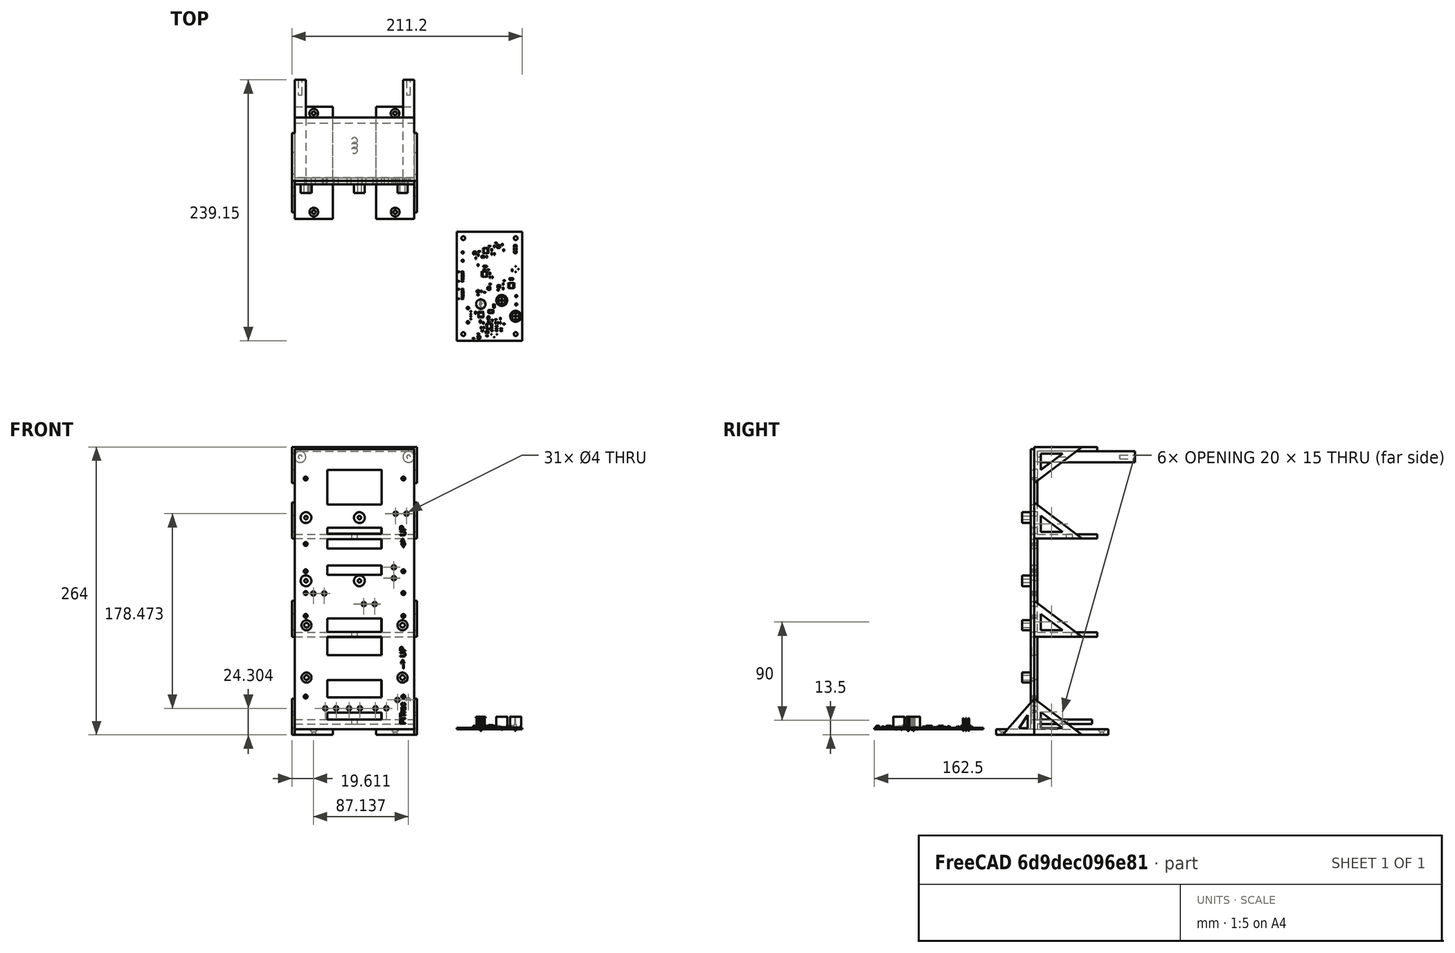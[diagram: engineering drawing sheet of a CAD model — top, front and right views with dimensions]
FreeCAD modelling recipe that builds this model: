
FCSTD DOCUMENT  (FreeCAD 1.0R39109 (Git))
Label: Tower
License: All rights reserved
LicenseURL: http://en.wikipedia.org/wiki/All_rights_reserved
objects: Part::Feature×73, Sketcher::SketchObject×17, PartDesign::Pad×9, PartDesign::Plane×9, PartDesign::Pocket×5, PartDesign::Hole×3, PartDesign::Mirrored×2, PartDesign::Body×2, App::Part×2, App::Link×1, Part::Part2DObjectPython×1
note: 174 computed .brp shape members not serialized (recipe doc carries the construction recipe); baked Part::Feature solids carry a one-line shape summary decoded from their .brp
EXTERNAL_REF file=../Master Document.FCStd obj=Spreadsheet

FEATURE [App::Link] Link  label="Monitor Chassis Parameters"
  LinkedObject = -> <external ../Master Document.FCStd>#Spreadsheet
FEATURE [Sketcher::SketchObject] Sketch  label="Backplate Sketch"
  ArcFitTolerance = 1e-06
  AttachmentSupport = -> [XZ_Plane001]
  FullyConstrained = false
  MakeInternals = false
  MapMode = 5
  Placement = pos=(0,0,0) rot=(1,0,0;1.5708rad)
  expr: Constraints[10] = <<Monitor Chassis Parameters>>.GSBackPlateBoltDiameter
  expr: Constraints[11] = <<Monitor Chassis Parameters>>.GSComputeBoardWidth / 2 - <<Monitor Chassis Parameters>>.GSBackPlateOuterHolesInsetFromSide
  expr: Constraints[129] = <<Monitor Chassis Parameters>>.GSTowerTieDownHoleSeparation
  expr: Constraints[15] = <<Monitor Chassis Parameters>>.GSBackPlateWidthIncrement
  expr: Constraints[55] = <<Monitor Chassis Parameters>>.GSBackPlateLengthIncrement
  expr: Constraints[59] = <<Monitor Chassis Parameters>>.GSBackPlateWidth
  expr: Constraints[71] = 1.5 * <<Monitor Chassis Parameters>>.GSBackPlateMinimumSpanWidth
  expr: Constraints[72] = 1.5 * <<Monitor Chassis Parameters>>.GSBackPlateMinimumSpanWidth
  expr: Constraints[7] = <<Monitor Chassis Parameters>>.GSComputeBoardHeight
  expr: Constraints[80] = <<Monitor Chassis Parameters>>.GSBackPlateLengthIncrement
  expr: Constraints[8] = <<Monitor Chassis Parameters>>.GSComputeBoardWidth
  expr: Constraints[97] = <<Monitor Chassis Parameters>>.GSTowerTieDownHoleDiameter
  expr: Constraints[98] = <<Monitor Chassis Parameters>>.GSTowerTieDownHoleDiameter
  expr: Constraints[99] = <<Monitor Chassis Parameters>>.GSTowerTieDownHoleSeparation
  expr: Constraints[9] = <<Monitor Chassis Parameters>>.GSComputeBoardWidth / 2
  sketch-geometry (63):
    g0: LineSegment [constr] StartX=-50.8 StartY=24.4067 StartZ=0 EndX=50.8 EndY=24.4067 EndZ=0
    g1: LineSegment [constr] StartX=50.8 StartY=24.4067 StartZ=0 EndX=50.8 EndY=253.007 EndZ=0
    g2: LineSegment [constr] StartX=50.8 StartY=253.007 StartZ=0 EndX=-50.8 EndY=253.007 EndZ=0
    g3: LineSegment [constr] StartX=-50.8 StartY=253.007 StartZ=0 EndX=-50.8 EndY=24.4067 EndZ=0
    g4: Circle CenterX=46.99 CenterY=45.5 CenterZ=0 NormalX=0 NormalY=0 NormalZ=1 AngleXU=0 Radius=1.4
    g5: LineSegment StartX=-54.8 StartY=257.007 StartZ=0 EndX=-54.8 EndY=20.4067 EndZ=0
    g6: LineSegment [constr] StartX=-54.8 StartY=20.4067 StartZ=0 EndX=54.8 EndY=20.4067 EndZ=0
    g7: LineSegment StartX=24.8 StartY=141.727 StartZ=0 EndX=-24.8 EndY=141.727 EndZ=0
    g8: LineSegment StartX=-24.8 StartY=141.727 StartZ=0 EndX=-24.8 EndY=150.228 EndZ=0
    g9: LineSegment StartX=-24.8 StartY=150.228 StartZ=0 EndX=24.8 EndY=150.228 EndZ=0
    g10: LineSegment StartX=24.8 StartY=150.228 StartZ=0 EndX=24.8 EndY=141.727 EndZ=0
    g11: LineSegment StartX=24.8 StartY=238.088 StartZ=0 EndX=-24.8 EndY=238.088 EndZ=0
    g12: LineSegment StartX=-24.8 StartY=238.088 StartZ=0 EndX=-24.8 EndY=206.336 EndZ=0
    g13: LineSegment StartX=-24.8 StartY=206.336 StartZ=0 EndX=24.8 EndY=206.336 EndZ=0
    g14: LineSegment StartX=24.8 StartY=206.336 StartZ=0 EndX=24.8 EndY=238.088 EndZ=0
    g15: LineSegment StartX=-24.8 StartY=184.895 StartZ=0 EndX=-24.8 EndY=179.263 EndZ=0
    g16: LineSegment StartX=-24.8 StartY=179.263 StartZ=0 EndX=24.8 EndY=179.263 EndZ=0
    g17: LineSegment StartX=24.8 StartY=179.263 StartZ=0 EndX=24.8 EndY=184.895 EndZ=0
    g18: LineSegment StartX=24.8 StartY=184.895 StartZ=0 EndX=-24.8 EndY=184.895 EndZ=0
    g19: LineSegment StartX=-24.8 StartY=84.8648 StartZ=0 EndX=-24.8 EndY=68.0887 EndZ=0
    g20: LineSegment StartX=-24.8 StartY=68.0887 StartZ=0 EndX=24.8 EndY=68.0887 EndZ=0
    g21: LineSegment StartX=24.8 StartY=68.0887 StartZ=0 EndX=24.8 EndY=84.8648 EndZ=0
    g22: LineSegment StartX=24.8 StartY=84.8648 StartZ=0 EndX=-24.8 EndY=84.8648 EndZ=0
    g23: LineSegment StartX=-24.8 StartY=45.1663 StartZ=0 EndX=-24.8 EndY=29.2968 EndZ=0
    g24: LineSegment StartX=24.8 StartY=29.2968 StartZ=0 EndX=24.8 EndY=45.1663 EndZ=0
    g25: LineSegment StartX=54.8 StartY=20.4067 StartZ=0 EndX=54.8 EndY=257.007 EndZ=0
    g26: LineSegment StartX=-54.8 StartY=257.007 StartZ=0 EndX=54.8 EndY=257.007 EndZ=0
    g27: LineSegment StartX=-54.8 StartY=20.4067 StartZ=0 EndX=-54.8 EndY=0 EndZ=0
    g28: LineSegment StartX=-54.8 StartY=0 StartZ=0 EndX=54.8 EndY=0 EndZ=0
    g29: LineSegment StartX=54.8 StartY=0 StartZ=0 EndX=54.8 EndY=20.4067 EndZ=0
    g30: LineSegment [constr] StartX=54.8 StartY=20.4067 StartZ=0 EndX=-54.8 EndY=20.4067 EndZ=0
    g31: LineSegment StartX=-24.8 StartY=45.1663 StartZ=0 EndX=24.8 EndY=45.1663 EndZ=0
    g32: LineSegment StartX=-24.8 StartY=29.2968 StartZ=0 EndX=24.8 EndY=29.2968 EndZ=0
    g33: LineSegment StartX=-24.8 StartY=15.5143 StartZ=0 EndX=-24.8 EndY=9.05652 EndZ=0
    g34: LineSegment StartX=-24.8 StartY=9.05652 StartZ=0 EndX=24.8 EndY=9.05652 EndZ=0
    g35: LineSegment StartX=24.8 StartY=9.05652 StartZ=0 EndX=24.8 EndY=15.5143 EndZ=0
    g36: LineSegment StartX=24.8 StartY=15.5143 StartZ=0 EndX=-24.8 EndY=15.5143 EndZ=0
    g37: Circle CenterX=37.7226 CenterY=197.777 CenterZ=0 NormalX=0 NormalY=0 NormalZ=1 AngleXU=0 Radius=2
    g38: Circle CenterX=47.7226 CenterY=197.777 CenterZ=0 NormalX=0 NormalY=0 NormalZ=1 AngleXU=0 Radius=2
    g39: Circle CenterX=-4.99066 CenterY=19.304 CenterZ=0 NormalX=0 NormalY=0 NormalZ=1 AngleXU=0 Radius=2
    g40: Circle CenterX=5.00934 CenterY=19.304 CenterZ=0 NormalX=0 NormalY=0 NormalZ=1 AngleXU=0 Radius=2
    g41: Circle CenterX=19.2048 CenterY=19.304 CenterZ=0 NormalX=0 NormalY=0 NormalZ=1 AngleXU=0 Radius=2
    g42: Circle CenterX=29.2048 CenterY=19.304 CenterZ=0 NormalX=0 NormalY=0 NormalZ=1 AngleXU=0 Radius=2
    g43: Circle CenterX=39.3678 CenterY=26.9682 CenterZ=0 NormalX=0 NormalY=0 NormalZ=1 AngleXU=0 Radius=2
    g44: Circle CenterX=49.3678 CenterY=26.9682 CenterZ=0 NormalX=0 NormalY=0 NormalZ=1 AngleXU=0 Radius=2
    g45: Circle CenterX=-37.7708 CenterY=124.614 CenterZ=0 NormalX=0 NormalY=0 NormalZ=1 AngleXU=0 Radius=2
    g46: Circle CenterX=-27.7708 CenterY=124.614 CenterZ=0 NormalX=0 NormalY=0 NormalZ=1 AngleXU=0 Radius=2
    g47: Circle CenterX=-26.8243 CenterY=19.304 CenterZ=0 NormalX=0 NormalY=0 NormalZ=1 AngleXU=0 Radius=2
    g48: Circle CenterX=-16.8243 CenterY=19.304 CenterZ=0 NormalX=0 NormalY=0 NormalZ=1 AngleXU=0 Radius=2
    g49: Circle CenterX=36.1106 CenterY=138.665 CenterZ=0 NormalX=0 NormalY=0 NormalZ=1 AngleXU=0 Radius=2
    g50: Circle CenterX=36.1106 CenterY=148.665 CenterZ=0 NormalX=0 NormalY=0 NormalZ=1 AngleXU=0 Radius=2
    g51: Circle CenterX=49.3678 CenterY=26.9682 CenterZ=0 NormalX=0 NormalY=0 NormalZ=1 AngleXU=0 Radius=2
    g52: Circle CenterX=8.52821 CenterY=114.871 CenterZ=0 NormalX=0 NormalY=0 NormalZ=1 AngleXU=0 Radius=2
    g53: Circle CenterX=18.5282 CenterY=114.871 CenterZ=0 NormalX=0 NormalY=0 NormalZ=1 AngleXU=0 Radius=2
    g54: Circle CenterX=49.3678 CenterY=26.9682 CenterZ=0 NormalX=0 NormalY=0 NormalZ=1 AngleXU=0 Radius=2
    g55: LineSegment StartX=-24.8 StartY=174.457 StartZ=0 EndX=-24.8 EndY=165.919 EndZ=0
    g56: LineSegment StartX=-24.8 StartY=165.919 StartZ=0 EndX=24.8 EndY=165.919 EndZ=0
    g57: LineSegment StartX=24.8 StartY=165.919 StartZ=0 EndX=24.8 EndY=174.457 EndZ=0
    g58: LineSegment StartX=24.8 StartY=174.457 StartZ=0 EndX=-24.8 EndY=174.457 EndZ=0
    g59: LineSegment StartX=-24.8 StartY=101.627 StartZ=0 EndX=-24.8 EndY=89.2697 EndZ=0
    g60: LineSegment StartX=-24.8 StartY=89.2697 StartZ=0 EndX=24.8 EndY=89.2697 EndZ=0
    g61: LineSegment StartX=24.8 StartY=89.2697 StartZ=0 EndX=24.8 EndY=101.627 EndZ=0
    g62: LineSegment StartX=24.8 StartY=101.627 StartZ=0 EndX=-24.8 EndY=101.627 EndZ=0
  constraints (152):
    c: Coincident(g0,g1)
    c: Coincident(g1,g2)
    c: Coincident(g2,g3)
    c: Coincident(g3,g0)
    c: Horizontal(g2)
    c: Vertical(g1)
    c: Vertical(g3)
    c: DistanceY(g0,g2) = 228.6
    c: DistanceX(g0,g0) = 101.6
    c: DistanceX(g0,g-1) = 50.8
    c: Diameter(g4) = 2.8
    c: DistanceX(g-1,g4) = 46.99
    c: Coincident(g5,g6)
    c: Vertical(g5)
    c: Horizontal(g6)
    c: DistanceX(g5,g0) = 4
    c: Horizontal(g0)
    c: Coincident(g7,g8)
    c: Coincident(g8,g9)
    c: Coincident(g9,g10)
    c: Coincident(g10,g7)
    c: Horizontal(g7)
    c: Vertical(g8)
    c: Vertical(g10)
    c: Coincident(g11,g12)
    c: Coincident(g12,g13)
    c: Coincident(g13,g14)
    c: Coincident(g14,g11)
    c: Horizontal(g11)
    c: Horizontal(g13)
    c: Vertical(g12)
    c: Vertical(g14)
    c: Coincident(g15,g16)
    c: Coincident(g16,g17)
    c: Coincident(g17,g18)
    c: Coincident(g18,g15)
    c: Vertical(g15)
    c: Vertical(g17)
    c: Horizontal(g16)
    c: Coincident(g19,g20)
    c: Coincident(g20,g21)
    c: Coincident(g21,g22)
    c: Coincident(g22,g19)
    c: Vertical(g19)
    c: Vertical(g21)
    c: Horizontal(g20)
    c: Horizontal(g22)
    c: Vertical(g23)
    c: Vertical(g24)
    c: Vertical(g15,g19)
    c: Vertical(g19,g23)
    c: Vertical(g7,g21)
    c: Vertical(g21,g24)
    c: Coincident(g25,g6)
    c: Vertical(g25)
    c: DistanceY(g1,g25) = 4
    c: Horizontal(g5,g25)
    c: Coincident(g26,g5)
    c: Coincident(g26,g25)
    c: DistanceX(g5,g6) = 109.6
    c: Coincident(g27,g28)
    c: Coincident(g28,g29)
    c: Coincident(g29,g30)
    c: Coincident(g30,g27)
    c: Vertical(g27)
    c: Vertical(g29)
    c: Horizontal(g28)
    c: Horizontal(g30)
    c: Coincident(g27,g5)
    c: Horizontal(g28,g-1)
    c: Vertical(g29,g6)
    c: DistanceX(g5,g11) = 30
    c: DistanceX(g11,g25) = 30
    c: Horizontal(g9)
    c: Coincident(g31,g23)
    c: Coincident(g31,g24)
    c: Horizontal(g31)
    c: Vertical(g11,g15)
    c: Vertical(g11,g9)
    c: Vertical(g16,g9)
    c: DistanceY(g5,g0) = 4
    c: Coincident(g32,g23)
    c: Coincident(g32,g24)
    c: Horizontal(g32)
    c: Horizontal(g18)
    c: Vertical(g15,g8)
    c: Coincident(g33,g34)
    c: Coincident(g34,g35)
    c: Coincident(g35,g36)
    c: Coincident(g36,g33)
    c: Vertical(g33)
    c: Vertical(g35)
    c: Horizontal(g34)
    c: Horizontal(g36)
    c: Vertical(g23,g33)
    c: Vertical(g24,g35)
    c: Horizontal(g37,g38)
    c: Diameter(g37) = 4
    c: Diameter(g38) = 4
    c: DistanceX(g37,g38) = 10
    c: Horizontal(g39,g40)
    c: Diameter(g39) = 4
    c: Diameter(g40) = 4
    c: DistanceX(g39,g40) = 10
    c: Horizontal(g41,g42)
    c: Diameter(g41) = 4
    c: Diameter(g42) = 4
    c: DistanceX(g41,g42) = 10
    c: Horizontal(g43,g44)
    c: Diameter(g43) = 4
    c: Diameter(g44) = 4
    c: DistanceX(g43,g44) = 10
    c: Horizontal(g45,g46)
    c: Diameter(g45) = 4
    c: Diameter(g46) = 4
    c: DistanceX(g45,g46) = 10
    c: Horizontal(g47,g48)
    c: Diameter(g47) = 4
    c: Diameter(g48) = 4
    c: DistanceX(g47,g48) = 10
    c: Diameter(g49) = 4
    c: Diameter(g50) = 4
    c: Diameter(g51) = 4
    c: Horizontal(g52,g53)
    c: Diameter(g52) = 4
    c: Diameter(g53) = 4
    c: DistanceX(g52,g53) = 10
    c: Diameter(g54) = 4
    c: Vertical(g50,g49)
    c: DistanceY(g49,g50) = 10
    c: Horizontal(g48,g39)
    c: Horizontal(g40,g41)
    c: Coincident(g55,g56)
    c: Coincident(g56,g57)
    c: Coincident(g57,g58)
    c: Coincident(g58,g55)
    c: Vertical(g55)
    c: Vertical(g57)
    c: Horizontal(g56)
    c: Horizontal(g58)
    c: Vertical(g8,g55)
    c: Vertical(g9,g56)
    c: Coincident(g59,g60)
    c: Coincident(g60,g61)
    c: Coincident(g61,g62)
    c: Coincident(g62,g59)
    c: Vertical(g59)
    c: Vertical(g61)
    c: Horizontal(g60)
    c: Horizontal(g62)
    c: Vertical(g20,g60)
    c: Vertical(g19,g59)
FEATURE [PartDesign::Pad] Pad  label="Backplate Pad"
  Direction = (0,-1,2e-16)
  Length = 3
  Length2 = 10
  Placement = pos=(0,0,0) rot=(1,0,0;1.5708rad)
  Profile = -> Sketch
  ReferenceAxis = -> Sketch [N_Axis]
  Reversed = true
  Suppressed = false
  Type = 0
  expr: Length = <<Monitor Chassis Parameters>>.GSBackPlateThickness
FEATURE [Sketcher::SketchObject] Sketch001  label="Backplate Risers Sketch"
  ArcFitTolerance = 1e-06
  AttachmentSupport = -> [XZ_Plane001]
  FullyConstrained = false
  MakeInternals = false
  MapMode = 5
  Placement = pos=(0,0,0) rot=(1,0,0;1.5708rad)
  expr: Constraints[12] = <<Monitor Chassis Parameters>>.GSPi5MountingRiserOutsideDiameter
  expr: Constraints[13] = <<Monitor Chassis Parameters>>.GSPi5MountingRiserOutsideDiameter
  expr: Constraints[14] = <<Monitor Chassis Parameters>>.GSPi5MountingRiserOutsideDiameter
  expr: Constraints[18] = <<Monitor Chassis Parameters>>.GSPi5MountingHoleCenterLength
  expr: Constraints[19] = <<Monitor Chassis Parameters>>.GSPi5MountingRiserOutsideDiameter
  expr: Constraints[21] = <<Monitor Chassis Parameters>>.GsPi5MountingHoleDiameter
  expr: Constraints[25] = <<Monitor Chassis Parameters>>.GSConnectorBoardMountingRiserOutsideDiameter
  expr: Constraints[26] = <<Monitor Chassis Parameters>>.GSConnectorBoardMountingHoleDiameter
  expr: Constraints[28] = <<Monitor Chassis Parameters>>.GSConnectorBoardMountingRiserOutsideDiameter
  expr: Constraints[29] = <<Monitor Chassis Parameters>>.GSConnectorBoardMountingHoleDiameter
  expr: Constraints[31] = <<Monitor Chassis Parameters>>.GSConnectorBoardMountingRiserOutsideDiameter
  expr: Constraints[32] = <<Monitor Chassis Parameters>>.GSConnectorBoardMountingHoleDiameter
  expr: Constraints[34] = <<Monitor Chassis Parameters>>.GSConnectorBoardMountingRiserOutsideDiameter
  expr: Constraints[35] = <<Monitor Chassis Parameters>>.GSConnectorBoardMountingHoleDiameter
  expr: Constraints[38] = <<Monitor Chassis Parameters>>.GsV2ConnectorBoardMountingHoleSeparationX
  expr: Constraints[39] = <<Monitor Chassis Parameters>>.GsV2ConnectorBoardMountingHoleSeparationY
  expr: Constraints[40] = 0.5 * <<Monitor Chassis Parameters>>.GSComputeBoardWidth - 0.5 * (<<Monitor Chassis Parameters>>.GSComputeBoardWidth - <<Monitor Chassis Parameters>>.GsV2ConnectorBoardMountingHoleSeparationX)
  expr: Constraints[41] = <<Monitor Chassis Parameters>>.GSPi5MountingHoleCenterWidth
  expr: Constraints[44] = 20 + 0.5 * <<Monitor Chassis Parameters>>.GSComputeBoardWidth - 0.5 * (<<Monitor Chassis Parameters>>.GSComputeBoardWidth - <<Monitor Chassis Parameters>>.GSPi5MountingHoleCenterWidth)
  expr: Constraints[5] = <<Monitor Chassis Parameters>>.GsPi5MountingHoleDiameter
  expr: Constraints[6] = <<Monitor Chassis Parameters>>.GsPi5MountingHoleDiameter
  expr: Constraints[7] = <<Monitor Chassis Parameters>>.GsPi5MountingHoleDiameter
  sketch-geometry (20):
    g0: LineSegment [constr] StartX=-50.8 StartY=20 StartZ=0 EndX=50.8 EndY=20 EndZ=0
    g1: LineSegment [constr] StartX=50.8 StartY=20 StartZ=0 EndX=50.8 EndY=248.6 EndZ=0
    g2: LineSegment [constr] StartX=50.8 StartY=248.6 StartZ=0 EndX=-50.8 EndY=248.6 EndZ=0
    g3: LineSegment [constr] StartX=-50.8 StartY=248.6 StartZ=0 EndX=-50.8 EndY=20 EndZ=0
    g4: Circle CenterX=-44.5 CenterY=136.223 CenterZ=0 NormalX=0 NormalY=0 NormalZ=1 AngleXU=0 Radius=1.575
    g5: Circle CenterX=4.5 CenterY=136.223 CenterZ=0 NormalX=0 NormalY=0 NormalZ=1 AngleXU=0 Radius=1.575
    g6: Circle CenterX=-44.5 CenterY=194.223 CenterZ=0 NormalX=0 NormalY=0 NormalZ=1 AngleXU=0 Radius=1.575
    g7: Circle CenterX=-44.5 CenterY=194.223 CenterZ=0 NormalX=0 NormalY=0 NormalZ=1 AngleXU=0 Radius=4.95
    g8: Circle CenterX=-44.5 CenterY=136.223 CenterZ=0 NormalX=0 NormalY=0 NormalZ=1 AngleXU=0 Radius=4.95
    g9: Circle CenterX=4.5 CenterY=136.223 CenterZ=0 NormalX=0 NormalY=0 NormalZ=1 AngleXU=0 Radius=4.95
    g10: Circle CenterX=4.5 CenterY=194.223 CenterZ=0 NormalX=0 NormalY=0 NormalZ=1 AngleXU=0 Radius=4.95
    g11: Circle CenterX=4.5 CenterY=194.223 CenterZ=0 NormalX=0 NormalY=0 NormalZ=1 AngleXU=0 Radius=1.575
    g12: Circle CenterX=-44 CenterY=47.4737 CenterZ=0 NormalX=0 NormalY=0 NormalZ=1 AngleXU=0 Radius=2.125
    g13: Circle CenterX=-44 CenterY=47.4737 CenterZ=0 NormalX=0 NormalY=0 NormalZ=1 AngleXU=0 Radius=4.625
    g14: Circle CenterX=44 CenterY=47.4737 CenterZ=0 NormalX=0 NormalY=0 NormalZ=1 AngleXU=0 Radius=2.125
    g15: Circle CenterX=44 CenterY=47.4737 CenterZ=0 NormalX=0 NormalY=0 NormalZ=1 AngleXU=0 Radius=4.625
    g16: Circle CenterX=44 CenterY=95.4737 CenterZ=0 NormalX=0 NormalY=0 NormalZ=1 AngleXU=0 Radius=2.125
    g17: Circle CenterX=44 CenterY=95.4737 CenterZ=0 NormalX=0 NormalY=0 NormalZ=1 AngleXU=0 Radius=4.625
    g18: Circle CenterX=-44 CenterY=95.4737 CenterZ=0 NormalX=0 NormalY=0 NormalZ=1 AngleXU=0 Radius=2.125
    g19: Circle CenterX=-44 CenterY=95.4737 CenterZ=0 NormalX=0 NormalY=0 NormalZ=1 AngleXU=0 Radius=4.625
  constraints (45):
    c: Coincident(g0,g1)
    c: Coincident(g1,g2)
    c: Coincident(g3,g0)
    c: Vertical(g1)
    c: Vertical(g3)
    c: Diameter(g4) = 3.15
    c: Diameter(g5) = 3.15
    c: Diameter(g6) = 3.15
    c: Horizontal(g0)
    c: Coincident(g7,g6)
    c: Coincident(g8,g4)
    c: Coincident(g9,g5)
    c: Diameter(g9) = 9.9
    c: Diameter(g8) = 9.9
    c: Diameter(g7) = 9.9
    c: Horizontal(g5,g4)
    c: Horizontal(g2,g1)
    c: Vertical(g6,g4)
    c: DistanceY(g4,g6) = 58
    c: Diameter(g10) = 9.9
    c: Coincident(g11,g10)
    c: Diameter(g11) = 3.15
    c: Horizontal(g10,g6)
    c: Vertical(g10,g5)
    c: Coincident(g13,g12)
    c: Diameter(g13) = 9.25
    c: Diameter(g12) = 4.25
    c: Coincident(g15,g14)
    c: Diameter(g15) = 9.25
    c: Diameter(g14) = 4.25
    c: Coincident(g17,g16)
    c: Diameter(g17) = 9.25
    c: Diameter(g16) = 4.25
    c: Coincident(g19,g18)
    c: Diameter(g19) = 9.25
    c: Diameter(g18) = 4.25
    c: Horizontal(g16,g18)
    c: Horizontal(g14,g12)
    c: DistanceX(g18,g16) = 88
    c: DistanceY(g12,g18) = 48
    c: DistanceX(g18,g-1) = 44
    c: DistanceX(g6,g10) = 49
    c: Vertical(g12,g18)
    c: Vertical(g16,g14)
    c: DistanceX(g4,g-1) = 44.5
FEATURE [PartDesign::Pad] Pad001  label="Backplate Risers Pad"
  BaseFeature = -> Pad
  Direction = (0,-1,2e-16)
  Length = 8
  Length2 = 10
  Placement = pos=(0,0,0) rot=(1,0,0;1.5708rad)
  Profile = -> Sketch001
  ReferenceAxis = -> Sketch001 [N_Axis]
  Suppressed = false
  Type = 0
  expr: Length = <<Monitor Chassis Parameters>>.GSBackPlateConnectorBoardVariantStandoffHeight
FEATURE [Sketcher::SketchObject] Sketch002  label="Backplate Foot Sketch"
  ArcFitTolerance = 1e-06
  AttachmentSupport = -> [XZ_Plane001]
  FullyConstrained = true
  MakeInternals = false
  MapMode = 5
  Placement = pos=(0,0,0) rot=(1,0,0;1.5708rad)
  expr: Constraints[11] = <<Monitor Chassis Parameters>>.GSTowerFeetThickness
  expr: Constraints[21] = <<Monitor Chassis Parameters>>.GSTowerFeetThickness
  expr: Constraints[22] = <<Monitor Chassis Parameters>>.GSBackPlateFootWidth
  expr: Constraints[23] = 0.5 * <<Monitor Chassis Parameters>>.GSBackPlateWidth
  expr: Constraints[8] = <<Monitor Chassis Parameters>>.GSBackPlateFootWidth
  expr: Constraints[9] = 0.5 * <<Monitor Chassis Parameters>>.GSBackPlateWidth
  sketch-geometry (8):
    g0: LineSegment StartX=-54.8 StartY=-5 StartZ=0 EndX=-19.8 EndY=-5 EndZ=0
    g1: LineSegment StartX=-19.8 StartY=-5 StartZ=0 EndX=-19.8 EndY=0 EndZ=0
    g2: LineSegment StartX=-19.8 StartY=0 StartZ=0 EndX=-54.8 EndY=0 EndZ=0
    g3: LineSegment StartX=-54.8 StartY=0 StartZ=0 EndX=-54.8 EndY=-5 EndZ=0
    g4: LineSegment StartX=54.8 StartY=-5 StartZ=0 EndX=54.8 EndY=0 EndZ=0
    g5: LineSegment StartX=54.8 StartY=0 StartZ=0 EndX=19.8 EndY=0 EndZ=0
    g6: LineSegment StartX=19.8 StartY=0 StartZ=0 EndX=19.8 EndY=-5 EndZ=0
    g7: LineSegment StartX=19.8 StartY=-5 StartZ=0 EndX=54.8 EndY=-5 EndZ=0
  constraints (24):
    c: Coincident(g0,g1)
    c: Coincident(g1,g2)
    c: Coincident(g2,g3)
    c: Coincident(g3,g0)
    c: Horizontal(g0)
    c: Horizontal(g2)
    c: Vertical(g1)
    c: Vertical(g3)
    c: DistanceX(g2,g1) = 35
    c: DistanceX(g2,g-1) = 54.8
    c: Horizontal(g2,g-1)
    c: DistanceY(g0,g2) = 5
    c: Coincident(g4,g5)
    c: Coincident(g5,g6)
    c: Coincident(g6,g7)
    c: Coincident(g7,g4)
    c: Vertical(g4)
    c: Vertical(g6)
    c: Horizontal(g5)
    c: Horizontal(g7)
    c: Horizontal(g5,g-1)
    c: DistanceY(g4,g4) = 5
    c: DistanceX(g6,g4) = 35
    c: DistanceX(g-1,g4) = 54.8
FEATURE [PartDesign::Pad] Pad002  label="Backplate Foot Pad"
  BaseFeature = -> Pad001
  Direction = (0,-1,2e-16)
  Length = 32
  Length2 = 3
  Placement = pos=(0,0,0) rot=(1,0,0;1.5708rad)
  Profile = -> Sketch002
  ReferenceAxis = -> Sketch002 [N_Axis]
  Suppressed = false
  Type = 4
  expr: Length = <<Monitor Chassis Parameters>>.GSBackPlateFootLengthBackward
  expr: Length2 = <<Monitor Chassis Parameters>>.GSBackPlateThickness
FEATURE [Sketcher::SketchObject] Sketch003  label="Backplate Foot Screw Holes Sketch"
  ArcFitTolerance = 1e-06
  AttachmentSupport = -> [XY_Plane001]
  FullyConstrained = true
  MakeInternals = false
  MapMode = 5
  expr: Constraints[0] = 0.8 * <<Monitor Chassis Parameters>>.GSBackPlateFootLengthBackward
  expr: Constraints[1] = 0.5 * <<Monitor Chassis Parameters>>.GSBackPlateWidth - 0.5 * <<Monitor Chassis Parameters>>.GSBackPlateFootWidth
  expr: Constraints[2] = 0.5 * <<Monitor Chassis Parameters>>.GSBackPlateWidth - 0.5 * <<Monitor Chassis Parameters>>.GSBackPlateFootWidth
  expr: Constraints[3] = <<Monitor Chassis Parameters>>.GSTowerFeetScrewDiameter
  expr: Constraints[4] = <<Monitor Chassis Parameters>>.GSTowerFeetScrewDiameter
  sketch-geometry (2):
    g0: Circle CenterX=-37.3 CenterY=-25.6 CenterZ=0 NormalX=0 NormalY=0 NormalZ=1 AngleXU=0 Radius=1.7
    g1: Circle CenterX=37.3 CenterY=-25.6 CenterZ=0 NormalX=0 NormalY=0 NormalZ=1 AngleXU=0 Radius=1.7
  constraints (6):
    c: DistanceY(g0,g-1) = 25.6
    c: DistanceX(g0,g-1) = 37.3
    c: DistanceX(g-1,g1) = 37.3
    c: Diameter(g0) = 3.4
    c: Diameter(g1) = 3.4
    c: Horizontal(g1,g0)
FEATURE [PartDesign::Hole] Hole  label="Backplate Foot Screw Holes"
  BaseFeature = -> Pad002
  CustomThreadClearance = 0
  Depth = 25
  DepthType = 0
  Diameter = 3.4
  DrillForDepth = false
  DrillPoint = 1
  DrillPointAngle = 118
  HoleCutCountersinkAngle = 90
  HoleCutCustomValues = false
  HoleCutDepth = 0
  HoleCutDiameter = 8
  HoleCutType = 2
  ModelThread = false
  Placement = pos=(0,0,0) rot=(1,0,0;1.5708rad)
  Profile = -> Sketch003
  Suppressed = false
  Tapered = false
  TaperedAngle = 90
  ThreadClass = 0
  ThreadDepth = 25
  ThreadDepthType = 0
  ThreadDirection = 0
  ThreadFit = 0
  ThreadSize = 0
  ThreadType = 0
  Threaded = false
  UseCustomThreadClearance = false
  expr: Diameter = <<Monitor Chassis Parameters>>.GSTowerFeetScrewDiameter
  expr: HoleCutDiameter = <<Monitor Chassis Parameters>>.GSM4BoltCountersinkDiameter
FEATURE [PartDesign::Plane] DatumPlane
  AttachmentOffset = pos=(0,0,54.8) rot=(0,0,1;0rad)
  AttachmentSupport = -> [YZ_Plane001]
  Length = 73.939
  MapMode = 5
  Placement = pos=(54.8,0,0) rot=(0.57735,0.57735,0.57735;2.0944rad)
  ResizeMode = 0
  Width = 245.788
  expr: .AttachmentOffset.Base.z = 0.5 * <<Monitor Chassis Parameters>>.GSBackPlateWidth
FEATURE [Sketcher::SketchObject] Sketch004  label="Foot Support Corner Sketch"
  ArcFitTolerance = 1e-06
  AttachmentSupport = -> [DatumPlane]
  FullyConstrained = true
  MakeInternals = false
  MapMode = 5
  Placement = pos=(54.8,0,0) rot=(0.57735,0.57735,0.57735;2.0944rad)
  expr: Constraints[14] = <<Monitor Chassis Parameters>>.GSSideCornerCutoutInset
  expr: Constraints[15] = <<Monitor Chassis Parameters>>.GSSideCornerCutoutInset
  expr: Constraints[16] = 2.5 * <<Monitor Chassis Parameters>>.GSSideCornerCutoutInset
  expr: Constraints[17] = 2.5 * <<Monitor Chassis Parameters>>.GSSideCornerCutoutInset
  expr: Constraints[1] = <<Monitor Chassis Parameters>>.GSBackPlateThickness
  expr: Constraints[4] = <<Monitor Chassis Parameters>>.GSTowerFeetThickness
  expr: Constraints[7] = 0.9 * <<Monitor Chassis Parameters>>.GSBackPlateFootLengthBackward
  expr: Constraints[8] = 0.6 * <<Monitor Chassis Parameters>>.GSTowerFloorDepth
  sketch-geometry (6):
    g0: LineSegment StartX=-25.8 StartY=-5 StartZ=0 EndX=3 EndY=-5 EndZ=0
    g1: LineSegment StartX=3 StartY=28 StartZ=0 EndX=3 EndY=-5 EndZ=0
    g2: LineSegment StartX=-25.8 StartY=-5 StartZ=0 EndX=3 EndY=28 EndZ=0
    g3: LineSegment StartX=-10.8 StartY=1 StartZ=0 EndX=-3 EndY=13 EndZ=0
    g4: LineSegment StartX=-3 StartY=13 StartZ=0 EndX=-3 EndY=1 EndZ=0
    g5: LineSegment StartX=-10.8 StartY=1 StartZ=0 EndX=-3 EndY=1 EndZ=0
  constraints (18):
    c: Horizontal(g0)
    c: DistanceX(g-1,g0) = 3
    c: Coincident(g1,g0)
    c: Vertical(g1)
    c: DistanceY(g0,g-1) = 5
    c: Coincident(g2,g0)
    c: Coincident(g2,g1)
    c: DistanceX(g0,g0) = 28.8
    c: DistanceY(g0,g1) = 33
    c: Coincident(g4,g3)
    c: Vertical(g4)
    c: Coincident(g5,g3)
    c: Coincident(g5,g4)
    c: Horizontal(g5)
    c: DistanceY(g0,g4) = 6
    c: DistanceX(g4,g0) = 6
    c: DistanceX(g0,g3) = 15
    c: DistanceY(g3,g1) = 15
FEATURE [PartDesign::Pad] Pad003  label="Foot Support Corner Pad"
  BaseFeature = -> Hole
  Direction = (1,0,0)
  Length = 2.5
  Length2 = 10
  Placement = pos=(0,0,0) rot=(1,0,0;1.5708rad)
  Profile = -> Sketch004
  ReferenceAxis = -> Sketch004 [N_Axis]
  Suppressed = false
  Type = 0
  expr: Length = <<Monitor Chassis Parameters>>.GSSideCornerThickness
FEATURE [PartDesign::Mirrored] Mirrored  label="Foot Support Corner Mirrored"
  BaseFeature = -> Pad003
  MirrorPlane = -> YZ_Plane001
  Originals = -> [Pad003]
  Placement = pos=(0,0,0) rot=(1,0,0;1.5708rad)
  Suppressed = false
  TransformMode = 0
FEATURE [PartDesign::Plane] DatumPlane001
  AttachmentOffset = pos=(0,0,54.8) rot=(0,0,1;0rad)
  AttachmentSupport = -> [YZ_Plane002]
  Length = 82.8329
  MapMode = 5
  Placement = pos=(54.8,0,0) rot=(0.57735,0.57735,0.57735;2.0944rad)
  ResizeMode = 0
  Width = 201.085
  expr: .AttachmentOffset.Base.z = 0.5 * <<Monitor Chassis Parameters>>.GSBackPlateWidth
FEATURE [Sketcher::SketchObject] Sketch005  label="Frontplate Sketch"
  ArcFitTolerance = 1e-06
  AttachmentSupport = -> [XZ_Plane002]
  FullyConstrained = false
  MakeInternals = false
  MapMode = 5
  Placement = pos=(0,0,0) rot=(1,0,0;1.5708rad)
  expr: Constraints[103] = <<Monitor Chassis Parameters>>.GSTowerLayerJoinScrewDiameter
  expr: Constraints[104] = <<Monitor Chassis Parameters>>.GSTowerLayerJoinScrewDiameter
  expr: Constraints[106] = <<Monitor Chassis Parameters>>.GSTowerLayerJoinScrewHeightFromFoot_1
  expr: Constraints[107] = <<Monitor Chassis Parameters>>.GSTowerLayerJoinScrewHeightFromFoot_3
  expr: Constraints[109] = <<Monitor Chassis Parameters>>.GSTowerLayerJoinScrewHeightFromFoot_4
  expr: Constraints[110] = <<Monitor Chassis Parameters>>.GSTowerLayerJoinScrewHeightFromFoot_5
  expr: Constraints[112] = <<Monitor Chassis Parameters>>.GSTowerLayerJoinScrewDiameter
  expr: Constraints[113] = <<Monitor Chassis Parameters>>.GSTowerLayerJoinScrewDiameter
  expr: Constraints[116] = <<Monitor Chassis Parameters>>.GSTowerLayerJoinScrewHeightFromFoot_6
  expr: Constraints[128] = <<Monitor Chassis Parameters>>.GSTowerLayerJoinScrewDiameter
  expr: Constraints[133] = <<Monitor Chassis Parameters>>.GSTowerLayerJoinScrewHeightFromFoot_2
  expr: Constraints[134] = <<Monitor Chassis Parameters>>.GSTowerTieDownHoleDiameter
  expr: Constraints[135] = <<Monitor Chassis Parameters>>.GSTowerTieDownHoleDiameter
  expr: Constraints[13] = <<Monitor Chassis Parameters>>.GSBackPlateWidthIncrement
  expr: Constraints[141] = <<Monitor Chassis Parameters>>.GSTowerTieDownHoleSeparation
  expr: Constraints[60] = <<Monitor Chassis Parameters>>.GSBackPlateLengthIncrement
  expr: Constraints[64] = <<Monitor Chassis Parameters>>.GSBackPlateWidth
  expr: Constraints[65] = <<Monitor Chassis Parameters>>.GSBackPlateVerticalOffset
  expr: Constraints[7] = <<Monitor Chassis Parameters>>.GSComputeBoardHeight
  expr: Constraints[84] = 1.5 * <<Monitor Chassis Parameters>>.GSFrontPlateMinimumSpanWidth
  expr: Constraints[85] = 1.5 * <<Monitor Chassis Parameters>>.GSFrontPlateMinimumSpanWidth
  expr: Constraints[89] = <<Monitor Chassis Parameters>>.GSTowerFourthFloorHeight + <<Monitor Chassis Parameters>>.GSTowerFloorThickness
  expr: Constraints[8] = <<Monitor Chassis Parameters>>.GSComputeBoardWidth
  expr: Constraints[90] = <<Monitor Chassis Parameters>>.GSTowerLayerJoinScrewDiameter
  expr: Constraints[91] = <<Monitor Chassis Parameters>>.GSTowerLayerJoinScrewDiameter
  expr: Constraints[93] = <<Monitor Chassis Parameters>>.GSTowerLayerJoinScrewInset
  expr: Constraints[94] = <<Monitor Chassis Parameters>>.GSTowerLayerJoinScrewInset
  expr: Constraints[95] = <<Monitor Chassis Parameters>>.GSTowerLayerJoinScrewDiameter
  expr: Constraints[96] = <<Monitor Chassis Parameters>>.GSTowerLayerJoinScrewDiameter
  expr: Constraints[98] = <<Monitor Chassis Parameters>>.GSTowerLayerJoinScrewDiameter
  expr: Constraints[99] = <<Monitor Chassis Parameters>>.GSTowerLayerJoinScrewDiameter
  expr: Constraints[9] = <<Monitor Chassis Parameters>>.GSComputeBoardWidth / 2
  sketch-geometry (75):
    g0: LineSegment [constr] StartX=-50.8 StartY=24 StartZ=0 EndX=50.8 EndY=24 EndZ=0
    g1: LineSegment [constr] StartX=50.8 StartY=24 StartZ=0 EndX=50.8 EndY=252.6 EndZ=0
    g2: LineSegment [constr] StartX=50.8 StartY=252.6 StartZ=0 EndX=-50.8 EndY=252.6 EndZ=0
    g3: LineSegment [constr] StartX=-50.8 StartY=252.6 StartZ=0 EndX=-50.8 EndY=24 EndZ=0
    g4: LineSegment StartX=-54.8 StartY=256.6 StartZ=0 EndX=-54.8 EndY=20 EndZ=0
    g5: LineSegment [constr] StartX=-54.8 StartY=20 StartZ=0 EndX=54.8 EndY=20 EndZ=0
    g6: LineSegment StartX=24.8 StartY=185.058 StartZ=0 EndX=-24.8 EndY=185.058 EndZ=0
    g7: LineSegment StartX=-24.8 StartY=185.058 StartZ=0 EndX=-24.8 EndY=179.38 EndZ=0
    g8: LineSegment StartX=-24.8 StartY=179.38 StartZ=0 EndX=24.8 EndY=179.38 EndZ=0
    g9: LineSegment StartX=24.8 StartY=179.38 StartZ=0 EndX=24.8 EndY=185.058 EndZ=0
    g10: LineSegment StartX=24.8 StartY=141.478 StartZ=0 EndX=-24.8 EndY=141.478 EndZ=0
    g11: LineSegment StartX=-24.8 StartY=141.478 StartZ=0 EndX=-24.8 EndY=150.178 EndZ=0
    g12: LineSegment StartX=-24.8 StartY=150.178 StartZ=0 EndX=24.8 EndY=150.178 EndZ=0
    g13: LineSegment StartX=24.8 StartY=150.178 StartZ=0 EndX=24.8 EndY=141.478 EndZ=0
    g14: LineSegment StartX=24.8 StartY=238.453 StartZ=0 EndX=-24.9755 EndY=238.453 EndZ=0
    g15: LineSegment StartX=-24.9755 StartY=238.453 StartZ=0 EndX=-24.9755 EndY=206.288 EndZ=0
    g16: LineSegment StartX=-24.9755 StartY=206.288 StartZ=0 EndX=24.8 EndY=206.288 EndZ=0
    g17: LineSegment StartX=24.8 StartY=206.288 StartZ=0 EndX=24.8 EndY=238.453 EndZ=0
    g18: LineSegment StartX=-24.8 StartY=45.5713 StartZ=0 EndX=-24.8 EndY=29.1792 EndZ=0
    g19: LineSegment StartX=-24.8 StartY=29.1792 StartZ=0 EndX=24.8 EndY=29.1792 EndZ=0
    g20: LineSegment StartX=24.8 StartY=29.1792 StartZ=0 EndX=24.8 EndY=45.5713 EndZ=0
    g21: LineSegment StartX=24.8 StartY=45.5713 StartZ=0 EndX=-24.8 EndY=45.5713 EndZ=0
    g22: LineSegment StartX=-24.8 StartY=15.6864 StartZ=0 EndX=-24.8 EndY=9.07096 EndZ=0
    g23: LineSegment StartX=-24.8 StartY=9.07096 StartZ=0 EndX=24.8 EndY=9.07096 EndZ=0
    g24: LineSegment StartX=24.8 StartY=9.07096 StartZ=0 EndX=24.8 EndY=15.6864 EndZ=0
    g25: LineSegment StartX=24.8 StartY=15.6864 StartZ=0 EndX=-24.8 EndY=15.6864 EndZ=0
    g26: LineSegment StartX=54.8 StartY=20 StartZ=0 EndX=54.8 EndY=256.6 EndZ=0
    g27: LineSegment [constr] StartX=-54.8 StartY=256.6 StartZ=0 EndX=54.8 EndY=256.6 EndZ=0
    g28: LineSegment StartX=-54.8 StartY=20 StartZ=0 EndX=-54.8 EndY=0 EndZ=0
    g29: LineSegment StartX=-54.8 StartY=0 StartZ=0 EndX=54.8 EndY=0 EndZ=0
    g30: LineSegment StartX=54.8 StartY=0 StartZ=0 EndX=54.8 EndY=20 EndZ=0
    g31: LineSegment [constr] StartX=54.8 StartY=20 StartZ=0 EndX=-54.8 EndY=20 EndZ=0
    g32: LineSegment StartX=-54.8 StartY=256.6 StartZ=0 EndX=-54.8 EndY=259 EndZ=0
    g33: LineSegment StartX=-54.8 StartY=259 StartZ=0 EndX=54.8 EndY=259 EndZ=0
    g34: LineSegment StartX=54.8 StartY=259 StartZ=0 EndX=54.8 EndY=256.6 EndZ=0
    g35: Circle CenterX=-44.8 CenterY=30 CenterZ=0 NormalX=0 NormalY=0 NormalZ=1 AngleXU=0 Radius=0.855
    g36: Circle CenterX=44.8 CenterY=30 CenterZ=0 NormalX=0 NormalY=0 NormalZ=1 AngleXU=0 Radius=0.855
    g37: Circle CenterX=-44.8 CenterY=125 CenterZ=0 NormalX=0 NormalY=0 NormalZ=1 AngleXU=0 Radius=0.855
    g38: Circle CenterX=44.8 CenterY=125 CenterZ=0 NormalX=0 NormalY=0 NormalZ=1 AngleXU=0 Radius=0.855
    g39: Circle CenterX=-44.8 CenterY=170 CenterZ=0 NormalX=0 NormalY=0 NormalZ=1 AngleXU=0 Radius=0.855
    g40: Circle CenterX=44.8 CenterY=170 CenterZ=0 NormalX=0 NormalY=0 NormalZ=1 AngleXU=0 Radius=0.855
    g41: Circle CenterX=-44.8 CenterY=145 CenterZ=0 NormalX=0 NormalY=0 NormalZ=1 AngleXU=0 Radius=0.855
    g42: Circle CenterX=44.8 CenterY=145 CenterZ=0 NormalX=0 NormalY=0 NormalZ=1 AngleXU=0 Radius=0.855
    g43: Circle CenterX=-44.8 CenterY=230 CenterZ=0 NormalX=0 NormalY=0 NormalZ=1 AngleXU=0 Radius=0.855
    g44: Circle CenterX=44.8 CenterY=230 CenterZ=0 NormalX=0 NormalY=0 NormalZ=1 AngleXU=0 Radius=0.855
    g45: LineSegment StartX=-24.8 StartY=68.1188 StartZ=0 EndX=24.8 EndY=68.1188 EndZ=0
    g46: LineSegment StartX=24.8 StartY=68.1188 StartZ=0 EndX=24.8 EndY=84.7075 EndZ=0
    g47: LineSegment StartX=24.8 StartY=84.7075 StartZ=0 EndX=-24.8 EndY=84.7075 EndZ=0
    g48: LineSegment StartX=-24.8 StartY=84.7075 StartZ=0 EndX=-24.8 EndY=68.1188 EndZ=0
    g49: Circle CenterX=-44.8 CenterY=104 CenterZ=0 NormalX=0 NormalY=0 NormalZ=1 AngleXU=0 Radius=0.855
    g50: Circle CenterX=44.8 CenterY=104 CenterZ=0 NormalX=0 NormalY=0 NormalZ=1 AngleXU=0 Radius=0.85
    g51: Circle CenterX=26.7285 CenterY=19.305 CenterZ=0 NormalX=0 NormalY=0 NormalZ=1 AngleXU=0 Radius=2
    g52: Circle CenterX=16.7285 CenterY=19.305 CenterZ=0 NormalX=0 NormalY=0 NormalZ=1 AngleXU=0 Radius=2
    g53: Circle CenterX=-36.1991 CenterY=148.72 CenterZ=0 NormalX=0 NormalY=0 NormalZ=1 AngleXU=0 Radius=2
    g54: Circle CenterX=-36.1991 CenterY=138.72 CenterZ=0 NormalX=0 NormalY=0 NormalZ=1 AngleXU=0 Radius=2
    g55: Circle CenterX=37.6894 CenterY=124.612 CenterZ=0 NormalX=0 NormalY=0 NormalZ=1 AngleXU=0 Radius=2
    g56: Circle CenterX=27.6894 CenterY=124.612 CenterZ=0 NormalX=0 NormalY=0 NormalZ=1 AngleXU=0 Radius=2
    g57: Circle CenterX=-19.2979 CenterY=19.305 CenterZ=0 NormalX=0 NormalY=0 NormalZ=1 AngleXU=0 Radius=2
    g58: Circle CenterX=-29.2979 CenterY=19.305 CenterZ=0 NormalX=0 NormalY=0 NormalZ=1 AngleXU=0 Radius=2
    g59: Circle CenterX=4.92244 CenterY=19.305 CenterZ=0 NormalX=0 NormalY=0 NormalZ=1 AngleXU=0 Radius=2
    g60: Circle CenterX=-5.07756 CenterY=19.305 CenterZ=0 NormalX=0 NormalY=0 NormalZ=1 AngleXU=0 Radius=2
    g61: Circle CenterX=-8.62291 CenterY=114.905 CenterZ=0 NormalX=0 NormalY=0 NormalZ=1 AngleXU=0 Radius=2
    g62: Circle CenterX=-18.6229 CenterY=114.905 CenterZ=0 NormalX=0 NormalY=0 NormalZ=1 AngleXU=0 Radius=2
    g63: Circle CenterX=-37.8246 CenterY=197.703 CenterZ=0 NormalX=0 NormalY=0 NormalZ=1 AngleXU=0 Radius=2
    g64: Circle CenterX=-47.8246 CenterY=197.703 CenterZ=0 NormalX=0 NormalY=0 NormalZ=1 AngleXU=0 Radius=2
    g65: Circle CenterX=-39.4472 CenterY=26.999 CenterZ=0 NormalX=0 NormalY=0 NormalZ=1 AngleXU=0 Radius=2
    g66: Circle CenterX=-49.4472 CenterY=26.999 CenterZ=0 NormalX=0 NormalY=0 NormalZ=1 AngleXU=0 Radius=2
    g67: LineSegment StartX=24.8 StartY=174.315 StartZ=0 EndX=-24.8 EndY=174.315 EndZ=0
    g68: LineSegment StartX=-24.8 StartY=174.315 StartZ=0 EndX=-24.8 EndY=165.952 EndZ=0
    g69: LineSegment StartX=-24.8 StartY=165.952 StartZ=0 EndX=24.8 EndY=165.952 EndZ=0
    g70: LineSegment StartX=24.8 StartY=165.952 StartZ=0 EndX=24.8 EndY=174.315 EndZ=0
    g71: LineSegment StartX=-24.8 StartY=89.2998 StartZ=0 EndX=24.8 EndY=89.2998 EndZ=0
    g72: LineSegment StartX=24.8 StartY=89.2998 StartZ=0 EndX=24.8 EndY=101.642 EndZ=0
    g73: LineSegment StartX=24.8 StartY=101.642 StartZ=0 EndX=-24.8 EndY=101.642 EndZ=0
    g74: LineSegment StartX=-24.8 StartY=101.642 StartZ=0 EndX=-24.8 EndY=89.2998 EndZ=0
  constraints (188):
    c: Coincident(g0,g1)
    c: Coincident(g1,g2)
    c: Coincident(g2,g3)
    c: Coincident(g3,g0)
    c: Horizontal(g2)
    c: Vertical(g1)
    c: Vertical(g3)
    c: DistanceY(g0,g2) = 228.6
    c: DistanceX(g0,g0) = 101.6
    c: DistanceX(g0,g-1) = 50.8
    c: Coincident(g4,g5)
    c: Vertical(g4)
    c: Horizontal(g5)
    c: DistanceX(g4,g0) = 4
    c: Horizontal(g0)
    c: Coincident(g6,g7)
    c: Coincident(g7,g8)
    c: Coincident(g8,g9)
    c: Coincident(g9,g6)
    c: Horizontal(g6)
    c: Horizontal(g8)
    c: Vertical(g7)
    c: Vertical(g9)
    c: Coincident(g10,g11)
    c: Coincident(g11,g12)
    c: Coincident(g12,g13)
    c: Coincident(g13,g10)
    c: Horizontal(g10)
    c: Horizontal(g12)
    c: Vertical(g11)
    c: Vertical(g13)
    c: Coincident(g14,g15)
    c: Coincident(g15,g16)
    c: Coincident(g16,g17)
    c: Coincident(g17,g14)
    c: Horizontal(g14)
    c: Horizontal(g16)
    c: Vertical(g15)
    c: Vertical(g17)
    c: Coincident(g18,g19)
    c: Coincident(g19,g20)
    c: Coincident(g20,g21)
    c: Coincident(g21,g18)
    c: Vertical(g18)
    c: Vertical(g20)
    c: Horizontal(g19)
    c: Horizontal(g21)
    c: Coincident(g22,g23)
    c: Coincident(g23,g24)
    c: Coincident(g24,g25)
    c: Coincident(g25,g22)
    c: Vertical(g22)
    c: Vertical(g24)
    c: Horizontal(g23)
    c: Horizontal(g25)
    c: Vertical(g18,g22)
    c: Vertical(g10,g20)
    c: Vertical(g20,g24)
    c: Coincident(g26,g5)
    c: Vertical(g26)
    c: DistanceY(g1,g26) = 4
    c: Horizontal(g4,g26)
    c: Coincident(g27,g4)
    c: Coincident(g27,g26)
    c: DistanceX(g4,g5) = 109.6
    c: DistanceY(g-1,g5) = 20
    c: Coincident(g28,g29)
    c: Coincident(g29,g30)
    c: Coincident(g30,g31)
    c: Coincident(g31,g28)
    c: Vertical(g28)
    c: Vertical(g30)
    c: Horizontal(g29)
    c: Horizontal(g31)
    c: Coincident(g28,g4)
    c: Horizontal(g29,g-1)
    c: Vertical(g30,g5)
    c: Coincident(g32,g4)
    c: Vertical(g32)
    c: Coincident(g33,g32)
    c: Horizontal(g33)
    c: Coincident(g34,g33)
    c: Coincident(g34,g26)
    c: Vertical(g34)
    c: DistanceX(g28,g22) = 30
    c: DistanceX(g23,g29) = 30
    c: Vertical(g10,g18)
    c: Vertical(g11,g7)
    c: Vertical(g12,g8)
    c: DistanceY(g29,g33) = 259
    c: Diameter(g35) = 1.71
    c: Diameter(g36) = 1.71
    c: Horizontal(g36,g35)
    c: DistanceX(g4,g35) = 10
    c: DistanceX(g36,g5) = 10
    c: Diameter(g37) = 1.71
    c: Diameter(g38) = 1.71
    c: Horizontal(g38,g37)
    c: Diameter(g39) = 1.71
    c: Diameter(g40) = 1.71
    c: Horizontal(g40,g39)
    c: Vertical(g39,g35)
    c: Vertical(g40,g38)
    c: Diameter(g41) = 1.71
    c: Diameter(g42) = 1.71
    c: Horizontal(g42,g41)
    c: DistanceY(g-1,g35) = 30
    c: DistanceY(g-1,g37) = 125
    c: Vertical(g41,g37)
    c: DistanceY(g-1,g41) = 145
    c: DistanceY(g-1,g39) = 170
    c: Vertical(g38,g42)
    c: Diameter(g44) = 1.71
    c: Diameter(g43) = 1.71
    c: Vertical(g44,g40)
    c: Vertical(g43,g39)
    c: DistanceY(g-1,g43) = 230
    c: Horizontal(g44,g43)
    c: Coincident(g45,g46)
    c: Coincident(g46,g47)
    c: Coincident(g47,g48)
    c: Coincident(g48,g45)
    c: Horizontal(g45)
    c: Horizontal(g47)
    c: Vertical(g46)
    c: Vertical(g48)
    c: Vertical(g45,g18)
    c: Vertical(g45,g20)
    c: Diameter(g49) = 1.71
    c: Vertical(g37,g49)
    c: Diameter(g50) = 1.7
    c: Horizontal(g49,g50)
    c: Vertical(g50,g38)
    c: DistanceY(g-1,g49) = 104
    c: Diameter(g51) = 4
    c: Diameter(g52) = 4
    c: DistanceY(g54,g53) = 10
    c: Vertical(g54,g53)
    c: Diameter(g53) = 4
    c: Diameter(g54) = 4
    c: Horizontal(g51,g52)
    c: DistanceX(g52,g51) = 10
    c: Diameter(g55) = 4
    c: Diameter(g56) = 4
    c: Horizontal(g55,g56)
    c: DistanceX(g56,g55) = 10
    c: Diameter(g57) = 4
    c: Diameter(g58) = 4
    c: Horizontal(g57,g58)
    c: DistanceX(g58,g57) = 10
    c: Diameter(g59) = 4
    c: Diameter(g60) = 4
    c: Horizontal(g59,g60)
    c: DistanceX(g60,g59) = 10
    c: Diameter(g61) = 4
    c: Diameter(g62) = 4
    c: Horizontal(g61,g62)
    c: DistanceX(g62,g61) = 10
    c: Diameter(g63) = 4
    c: Diameter(g64) = 4
    c: Horizontal(g63,g64)
    c: DistanceX(g64,g63) = 10
    c: Diameter(g65) = 4
    c: Diameter(g66) = 4
    c: Horizontal(g65,g66)
    c: DistanceX(g66,g65) = 10
    c: Horizontal(g57,g60)
    c: Horizontal(g59,g52)
    c: Coincident(g67,g68)
    c: Coincident(g68,g69)
    c: Coincident(g69,g70)
    c: Coincident(g70,g67)
    c: Horizontal(g67)
    c: Horizontal(g69)
    c: Vertical(g68)
    c: Vertical(g70)
    c: Vertical(g68,g7)
    c: Vertical(g69,g8)
    c: Coincident(g71,g72)
    c: Coincident(g72,g73)
    c: Coincident(g73,g74)
    c: Coincident(g74,g71)
    c: Horizontal(g71)
    c: Horizontal(g73)
    c: Vertical(g72)
    c: Vertical(g74)
    c: Vertical(g45,g71)
    c: Vertical(g71,g45)
FEATURE [PartDesign::Pad] Pad004  label="Frontplate Pad"
  Direction = (0,-1,2e-16)
  Length = 3
  Length2 = 10
  Placement = pos=(0,0,0) rot=(1,0,0;1.5708rad)
  Profile = -> Sketch005
  ReferenceAxis = -> Sketch005 [N_Axis]
  Reversed = true
  Suppressed = false
  Type = 0
  expr: Length = <<Monitor Chassis Parameters>>.GSBackPlateThickness
FEATURE [Sketcher::SketchObject] Sketch007  label="Frontplate Foot Sketch"
  ArcFitTolerance = 1e-06
  AttachmentSupport = -> [XZ_Plane002]
  FullyConstrained = true
  MakeInternals = false
  MapMode = 5
  Placement = pos=(0,0,0) rot=(1,0,0;1.5708rad)
  expr: Constraints[11] = <<Monitor Chassis Parameters>>.GSTowerFeetThickness
  expr: Constraints[21] = <<Monitor Chassis Parameters>>.GSTowerFeetThickness
  expr: Constraints[22] = <<Monitor Chassis Parameters>>.GSBackPlateFootWidth
  expr: Constraints[23] = 0.5 * <<Monitor Chassis Parameters>>.GSBackPlateWidth
  expr: Constraints[8] = <<Monitor Chassis Parameters>>.GSBackPlateFootWidth
  expr: Constraints[9] = 0.5 * <<Monitor Chassis Parameters>>.GSBackPlateWidth
  sketch-geometry (8):
    g0: LineSegment StartX=-54.8 StartY=-5 StartZ=0 EndX=-19.8 EndY=-5 EndZ=0
    g1: LineSegment StartX=-19.8 StartY=-5 StartZ=0 EndX=-19.8 EndY=0 EndZ=0
    g2: LineSegment StartX=-19.8 StartY=0 StartZ=0 EndX=-54.8 EndY=0 EndZ=0
    g3: LineSegment StartX=-54.8 StartY=0 StartZ=0 EndX=-54.8 EndY=-5 EndZ=0
    g4: LineSegment StartX=54.8 StartY=-5 StartZ=0 EndX=54.8 EndY=0 EndZ=0
    g5: LineSegment StartX=54.8 StartY=0 StartZ=0 EndX=19.8 EndY=0 EndZ=0
    g6: LineSegment StartX=19.8 StartY=0 StartZ=0 EndX=19.8 EndY=-5 EndZ=0
    g7: LineSegment StartX=19.8 StartY=-5 StartZ=0 EndX=54.8 EndY=-5 EndZ=0
  constraints (24):
    c: Coincident(g0,g1)
    c: Coincident(g1,g2)
    c: Coincident(g2,g3)
    c: Coincident(g3,g0)
    c: Horizontal(g0)
    c: Horizontal(g2)
    c: Vertical(g1)
    c: Vertical(g3)
    c: DistanceX(g2,g1) = 35
    c: DistanceX(g2,g-1) = 54.8
    c: Horizontal(g2,g-1)
    c: DistanceY(g0,g2) = 5
    c: Coincident(g4,g5)
    c: Coincident(g5,g6)
    c: Coincident(g6,g7)
    c: Coincident(g7,g4)
    c: Vertical(g4)
    c: Vertical(g6)
    c: Horizontal(g5)
    c: Horizontal(g7)
    c: Horizontal(g5,g-1)
    c: DistanceY(g4,g4) = 5
    c: DistanceX(g6,g4) = 35
    c: DistanceX(g-1,g4) = 54.8
FEATURE [PartDesign::Pad] Pad006  label="Frontplate Foot Pad"
  BaseFeature = -> Pad004
  Direction = (0,-1,2e-16)
  Length = 65
  Length2 = 3
  Placement = pos=(0,0,0) rot=(1,0,0;1.5708rad)
  Profile = -> Sketch007
  ReferenceAxis = -> Sketch007 [N_Axis]
  Suppressed = false
  Type = 4
  expr: Length = <<Monitor Chassis Parameters>>.GSBackPlateFootLengthForward
  expr: Length2 = <<Monitor Chassis Parameters>>.GSBackPlateThickness
FEATURE [Sketcher::SketchObject] Sketch008  label="Frontplate Foot Screw Holes Sketch"
  ArcFitTolerance = 1e-06
  AttachmentSupport = -> [XY_Plane002]
  FullyConstrained = true
  MakeInternals = false
  MapMode = 5
  expr: Constraints[0] = <<Monitor Chassis Parameters>>.GSBackPlateFootScrewHoleForwardOffset
  expr: Constraints[1] = 0.5 * <<Monitor Chassis Parameters>>.GSBackPlateWidth - 0.5 * <<Monitor Chassis Parameters>>.GSBackPlateFootWidth
  expr: Constraints[2] = 0.5 * <<Monitor Chassis Parameters>>.GSBackPlateWidth - 0.5 * <<Monitor Chassis Parameters>>.GSBackPlateFootWidth
  expr: Constraints[3] = <<Monitor Chassis Parameters>>.GSTowerFeetScrewDiameter
  expr: Constraints[4] = <<Monitor Chassis Parameters>>.GSTowerFeetScrewDiameter
  sketch-geometry (2):
    g0: Circle CenterX=-37.3 CenterY=-59 CenterZ=0 NormalX=0 NormalY=0 NormalZ=1 AngleXU=0 Radius=1.7
    g1: Circle CenterX=37.3 CenterY=-59 CenterZ=0 NormalX=0 NormalY=0 NormalZ=1 AngleXU=0 Radius=1.7
  constraints (6):
    c: DistanceY(g0,g-1) = 59
    c: DistanceX(g0,g-1) = 37.3
    c: DistanceX(g-1,g1) = 37.3
    c: Diameter(g0) = 3.4
    c: Diameter(g1) = 3.4
    c: Horizontal(g1,g0)
FEATURE [PartDesign::Hole] Hole001  label="Frontplate Foot Screw Holes"
  BaseFeature = -> Pad006
  CustomThreadClearance = 0
  Depth = 25
  DepthType = 0
  Diameter = 3.4
  DrillForDepth = false
  DrillPoint = 1
  DrillPointAngle = 118
  HoleCutCountersinkAngle = 90
  HoleCutCustomValues = false
  HoleCutDepth = 0
  HoleCutDiameter = 8
  HoleCutType = 2
  ModelThread = false
  Placement = pos=(0,0,0) rot=(1,0,0;1.5708rad)
  Profile = -> Sketch008
  Suppressed = false
  Tapered = false
  TaperedAngle = 90
  ThreadClass = 0
  ThreadDepth = 25
  ThreadDepthType = 0
  ThreadDirection = 0
  ThreadFit = 0
  ThreadSize = 0
  ThreadType = 0
  Threaded = false
  UseCustomThreadClearance = false
  expr: Diameter = <<Monitor Chassis Parameters>>.GSTowerFeetScrewDiameter
  expr: HoleCutDiameter = <<Monitor Chassis Parameters>>.GSM4BoltCountersinkDiameter
FEATURE [Sketcher::SketchObject] Sketch009  label="Frontplate Foot Support Corner Sketch"
  ArcFitTolerance = 1e-06
  AttachmentSupport = -> [DatumPlane001]
  FullyConstrained = true
  MakeInternals = false
  MapMode = 5
  Placement = pos=(54.8,0,0) rot=(0.57735,0.57735,0.57735;2.0944rad)
  expr: Constraints[1] = <<Monitor Chassis Parameters>>.GSBackPlateThickness
  expr: Constraints[24] = 0.8 * <<Monitor Chassis Parameters>>.GSTowerFloorDepth
  expr: Constraints[25] = 0.6 * <<Monitor Chassis Parameters>>.GSTowerFloorDepth
  expr: Constraints[26] = <<Monitor Chassis Parameters>>.GSSideCornerCutoutInset
  expr: Constraints[27] = <<Monitor Chassis Parameters>>.GSSideCornerCutoutInset
  expr: Constraints[28] = 2 * <<Monitor Chassis Parameters>>.GSSideCornerCutoutInset
  expr: Constraints[29] = 3 * <<Monitor Chassis Parameters>>.GSSideCornerCutoutInset
  expr: Constraints[39] = 0.8 * <<Monitor Chassis Parameters>>.GSTowerFloorDepth
  expr: Constraints[3] = <<Monitor Chassis Parameters>>.GSTowerFeetThickness
  expr: Constraints[41] = <<Monitor Chassis Parameters>>.GSSideCornerCutoutInset
  expr: Constraints[42] = -2 * <<Monitor Chassis Parameters>>.GSSideCornerCutoutInset
  expr: Constraints[43] = 3 * <<Monitor Chassis Parameters>>.GSSideCornerCutoutInset
  expr: Constraints[54] = 0.8 * <<Monitor Chassis Parameters>>.GSTowerFloorDepth
  expr: Constraints[55] = 0.6 * <<Monitor Chassis Parameters>>.GSTowerFloorDepth
  expr: Constraints[56] = <<Monitor Chassis Parameters>>.GSSideCornerCutoutInset
  expr: Constraints[57] = <<Monitor Chassis Parameters>>.GSSideCornerCutoutInset
  expr: Constraints[58] = 2 * <<Monitor Chassis Parameters>>.GSSideCornerCutoutInset
  expr: Constraints[59] = 3 * <<Monitor Chassis Parameters>>.GSSideCornerCutoutInset
  expr: Constraints[62] = <<Monitor Chassis Parameters>>.GSTowerThirdFloorHeight
  expr: Constraints[63] = <<Monitor Chassis Parameters>>.GSTowerSecondFloorHeight
  expr: Constraints[64] = 0.6 * <<Monitor Chassis Parameters>>.GSTowerFloorDepth
  expr: Constraints[65] = <<Monitor Chassis Parameters>>.GSTowerFourthFloorHeight + <<Monitor Chassis Parameters>>.GSTowerFloorThickness
  expr: Constraints[6] = 0.8 * <<Monitor Chassis Parameters>>.GSTowerFloorDepth
  expr: Constraints[70] = 2 * <<Monitor Chassis Parameters>>.GSSideCornerCutoutInset
  expr: Constraints[71] = 3 * <<Monitor Chassis Parameters>>.GSSideCornerCutoutInset
  expr: Constraints[73] = <<Monitor Chassis Parameters>>.GSSideCornerCutoutInset
  expr: Constraints[7] = 0.6 * <<Monitor Chassis Parameters>>.GSTowerFloorDepth
  sketch-geometry (24):
    g0: LineSegment StartX=-41 StartY=-5 StartZ=0 EndX=3 EndY=-5 EndZ=0
    g1: LineSegment StartX=3 StartY=28 StartZ=0 EndX=3 EndY=-5 EndZ=0
    g2: LineSegment StartX=-41 StartY=-5 StartZ=0 EndX=3 EndY=28 EndZ=0
    g3: LineSegment StartX=-23 StartY=181 StartZ=0 EndX=-3 EndY=196 EndZ=0
    g4: LineSegment StartX=-3 StartY=196 StartZ=0 EndX=-3 EndY=181 EndZ=0
    g5: LineSegment StartX=-23 StartY=181 StartZ=0 EndX=-3 EndY=181 EndZ=0
    g6: LineSegment StartX=3 StartY=208 StartZ=0 EndX=3 EndY=175 EndZ=0
    g7: LineSegment StartX=3 StartY=175 StartZ=0 EndX=-41 EndY=175 EndZ=0
    g8: LineSegment StartX=-41 StartY=175 StartZ=0 EndX=3 EndY=208 EndZ=0
    g9: LineSegment StartX=-23 StartY=1 StartZ=0 EndX=-3 EndY=16 EndZ=0
    g10: LineSegment StartX=-3 StartY=16 StartZ=0 EndX=-3 EndY=1 EndZ=0
    g11: LineSegment StartX=-23 StartY=1 StartZ=0 EndX=-3 EndY=1 EndZ=0
    g12: LineSegment StartX=-23 StartY=253 StartZ=0 EndX=-3 EndY=238 EndZ=0
    g13: LineSegment StartX=-3 StartY=238 StartZ=0 EndX=-3 EndY=253 EndZ=0
    g14: LineSegment StartX=-23 StartY=253 StartZ=0 EndX=-3 EndY=253 EndZ=0
    g15: LineSegment StartX=3 StartY=226 StartZ=0 EndX=3 EndY=259 EndZ=0
    g16: LineSegment StartX=3 StartY=259 StartZ=0 EndX=-41 EndY=259 EndZ=0
    g17: LineSegment StartX=-41 StartY=259 StartZ=0 EndX=3 EndY=226 EndZ=0
    g18: LineSegment StartX=-23 StartY=91 StartZ=0 EndX=-3 EndY=106 EndZ=0
    g19: LineSegment StartX=-3 StartY=106 StartZ=0 EndX=-3 EndY=91 EndZ=0
    g20: LineSegment StartX=-23 StartY=91 StartZ=0 EndX=-3 EndY=91 EndZ=0
    g21: LineSegment StartX=3 StartY=118 StartZ=0 EndX=3 EndY=85 EndZ=0
    g22: LineSegment StartX=3 StartY=85 StartZ=0 EndX=-41 EndY=85 EndZ=0
    g23: LineSegment StartX=-41 StartY=85 StartZ=0 EndX=3 EndY=118 EndZ=0
  constraints (74):
    c: Horizontal(g0)
    c: DistanceX(g-1,g0) = 3
    c: Vertical(g1)
    c: DistanceY(g0,g-1) = 5
    c: Coincident(g2,g0)
    c: Coincident(g2,g1)
    c: DistanceX(g0,g0) = 44
    c: DistanceY(g0,g1) = 33
    c: Coincident(g4,g3)
    c: Vertical(g4)
    c: Coincident(g5,g3)
    c: Coincident(g5,g4)
    c: Horizontal(g5)
    c: Vertical(g6)
    c: Coincident(g7,g6)
    c: Horizontal(g7)
    c: Coincident(g8,g7)
    c: Coincident(g8,g6)
    c: Coincident(g10,g9)
    c: Vertical(g10)
    c: Coincident(g11,g9)
    c: Coincident(g11,g10)
    c: Horizontal(g11)
    c: Vertical(g6,g1)
    c: DistanceX(g7,g6) = 44
    c: DistanceY(g6,g6) = 33
    c: DistanceY(g6,g4) = 6
    c: DistanceX(g4,g6) = 6
    c: DistanceY(g3,g6) = 12
    c: DistanceX(g7,g3) = 18
    c: Coincident(g13,g12)
    c: Vertical(g13)
    c: Coincident(g14,g12)
    c: Coincident(g14,g13)
    c: Horizontal(g14)
    c: Vertical(g15)
    c: Horizontal(g16)
    c: Coincident(g17,g16)
    c: Coincident(g17,g15)
    c: DistanceX(g16,g15) = 44
    c: DistanceY(g15,g13) = -6
    c: DistanceX(g13,g15) = 6
    c: DistanceY(g12,g15) = -12
    c: DistanceX(g16,g12) = 18
    c: Coincident(g19,g18)
    c: Vertical(g19)
    c: Coincident(g20,g18)
    c: Coincident(g20,g19)
    c: Horizontal(g20)
    c: Vertical(g21)
    c: Coincident(g22,g21)
    c: Horizontal(g22)
    c: Coincident(g23,g22)
    c: Coincident(g23,g21)
    c: DistanceX(g22,g21) = 44
    c: DistanceY(g21,g21) = 33
    c: DistanceY(g21,g19) = 6
    c: DistanceX(g19,g21) = 6
    c: DistanceY(g18,g21) = 12
    c: DistanceX(g22,g18) = 18
    c: Vertical(g21,g6)
    c: Vertical(g6,g15)
    c: DistanceY(g-1,g6) = 175
    c: DistanceY(g-1,g21) = 85
    c: DistanceY(g15,g15) = 33
    c: DistanceY(g-1,g15) = 259
    c: Horizontal(g16,g15)
    c: Vertical(g16,g15)
    c: Vertical(g1,g0)
    c: Horizontal(g1,g0)
    c: DistanceY(g9,g1) = 12
    c: DistanceX(g0,g9) = 18
    c: Vertical(g19,g9)
    c: DistanceY(g0,g10) = 6
FEATURE [PartDesign::Pad] Pad007  label="Frontplate Floor Support Corner Pad"
  BaseFeature = -> Hole001
  Direction = (1,0,0)
  Length = 2.5
  Length2 = 10
  Placement = pos=(0,0,0) rot=(1,0,0;1.5708rad)
  Profile = -> Sketch009
  ReferenceAxis = -> Sketch009 [N_Axis]
  Suppressed = false
  Type = 0
  expr: Length = <<Monitor Chassis Parameters>>.GSSideCornerThickness
FEATURE [PartDesign::Mirrored] Mirrored001  label="Frontplate Floor Support Corner Mirrored"
  BaseFeature = -> Pad007
  MirrorPlane = -> YZ_Plane002
  Originals = -> [Pad007]
  Placement = pos=(0,0,0) rot=(1,0,0;1.5708rad)
  Suppressed = false
  TransformMode = 0
FEATURE [Sketcher::SketchObject] Sketch010  label="Frontplate Floors Sketch"
  ArcFitTolerance = 1e-06
  AttachmentSupport = -> [DatumPlane001]
  FullyConstrained = true
  MakeInternals = false
  MapMode = 5
  Placement = pos=(54.8,0,0) rot=(0.57735,0.57735,0.57735;2.0944rad)
  expr: Constraints[10] = <<Monitor Chassis Parameters>>.GSTowerSecondFloorDepth
  expr: Constraints[21] = <<Monitor Chassis Parameters>>.GSTowerFourthFloorDepth
  expr: Constraints[32] = <<Monitor Chassis Parameters>>.GSTowerThirdFloorDepth
  expr: Constraints[43] = <<Monitor Chassis Parameters>>.GSTowerFirstFloorDepth
  expr: Constraints[44] = <<Monitor Chassis Parameters>>.GSTowerFirstFloorHeight
  expr: Constraints[45] = <<Monitor Chassis Parameters>>.GSTowerSecondFloorHeight
  expr: Constraints[46] = <<Monitor Chassis Parameters>>.GSTowerFourthFloorHeight
  expr: Constraints[47] = <<Monitor Chassis Parameters>>.GSTowerThirdFloorHeight
  expr: Constraints[9] = <<Monitor Chassis Parameters>>.GSTowerFloorThickness
  sketch-geometry (16):
    g0: LineSegment StartX=-55 StartY=85 StartZ=0 EndX=0 EndY=85 EndZ=0
    g1: LineSegment StartX=0 StartY=85 StartZ=0 EndX=0 EndY=89 EndZ=0
    g2: LineSegment StartX=0 StartY=89 StartZ=0 EndX=-55 EndY=89 EndZ=0
    g3: LineSegment StartX=-55 StartY=89 StartZ=0 EndX=-55 EndY=85 EndZ=0
    g4: LineSegment StartX=-55 StartY=255 StartZ=0 EndX=0 EndY=255 EndZ=0
    g5: LineSegment StartX=0 StartY=255 StartZ=0 EndX=0 EndY=259 EndZ=0
    g6: LineSegment StartX=0 StartY=259 StartZ=0 EndX=-55 EndY=259 EndZ=0
    g7: LineSegment StartX=-55 StartY=259 StartZ=0 EndX=-55 EndY=255 EndZ=0
    g8: LineSegment StartX=-55 StartY=175 StartZ=0 EndX=0 EndY=175 EndZ=0
    g9: LineSegment StartX=0 StartY=175 StartZ=0 EndX=0 EndY=179 EndZ=0
    g10: LineSegment StartX=0 StartY=179 StartZ=0 EndX=-55 EndY=179 EndZ=0
    g11: LineSegment StartX=-55 StartY=179 StartZ=0 EndX=-55 EndY=175 EndZ=0
    g12: LineSegment StartX=-50 StartY=5 StartZ=0 EndX=0 EndY=5 EndZ=0
    g13: LineSegment StartX=0 StartY=5 StartZ=0 EndX=0 EndY=9 EndZ=0
    g14: LineSegment StartX=0 StartY=9 StartZ=0 EndX=-50 EndY=9 EndZ=0
    g15: LineSegment StartX=-50 StartY=9 StartZ=0 EndX=-50 EndY=5 EndZ=0
  constraints (48):
    c: Coincident(g0,g1)
    c: Coincident(g1,g2)
    c: Coincident(g2,g3)
    c: Coincident(g3,g0)
    c: Horizontal(g0)
    c: Horizontal(g2)
    c: Vertical(g1)
    c: Vertical(g3)
    c: Vertical(g0,g-1)
    c: DistanceY(g0,g2) = 4
    c: DistanceX(g2,g1) = 55
    c: Coincident(g4,g5)
    c: Coincident(g5,g6)
    c: Coincident(g6,g7)
    c: Coincident(g7,g4)
    c: Horizontal(g4)
    c: Horizontal(g6)
    c: Vertical(g5)
    c: Vertical(g7)
    c: Vertical(g4,g-1)
    c: DistanceY(g4,g6) = 4
    c: DistanceX(g6,g5) = 55
    c: Coincident(g8,g9)
    c: Coincident(g9,g10)
    c: Coincident(g10,g11)
    c: Coincident(g11,g8)
    c: Horizontal(g8)
    c: Horizontal(g10)
    c: Vertical(g9)
    c: Vertical(g11)
    c: Vertical(g8,g-1)
    c: DistanceY(g8,g10) = 4
    c: DistanceX(g10,g9) = 55
    c: Coincident(g12,g13)
    c: Coincident(g13,g14)
    c: Coincident(g14,g15)
    c: Coincident(g15,g12)
    c: Horizontal(g12)
    c: Horizontal(g14)
    c: Vertical(g13)
    c: Vertical(g15)
    c: Vertical(g12,g-1)
    c: DistanceY(g12,g14) = 4
    c: DistanceX(g14,g13) = 50
    c: DistanceY(g-1,g12) = 5
    c: DistanceY(g-1,g0) = 85
    c: DistanceY(g-1,g4) = 255
    c: DistanceY(g-1,g8) = 175
FEATURE [PartDesign::Pad] Pad008  label="Tower Floors Pad"
  BaseFeature = -> Mirrored001
  Direction = (1,0,0)
  Length = 109.6
  Length2 = 10
  Placement = pos=(0,0,0) rot=(1,0,0;1.5708rad)
  Profile = -> Sketch010
  ReferenceAxis = -> Sketch010 [N_Axis]
  Reversed = true
  Suppressed = false
  Type = 0
  expr: Length = <<Monitor Chassis Parameters>>.GSBackPlateWidth
FEATURE [PartDesign::Plane] DatumPlane002  label="First Floor DatumPlane"
  AttachmentOffset = pos=(0,0,9) rot=(0,0,1;0rad)
  AttachmentSupport = -> [XY_Plane002]
  Length = 61.1129
  MapMode = 5
  Placement = pos=(0,0,9) rot=(0,0,1;0rad)
  ResizeMode = 0
  Width = 72.8606
  expr: .AttachmentOffset.Base.z = <<Monitor Chassis Parameters>>.GSTowerFirstFloorHeight + <<Monitor Chassis Parameters>>.GSTowerFloorThickness
FEATURE [PartDesign::Plane] DatumPlane003  label="Second Floor DatumPlane"
  AttachmentOffset = pos=(0,0,89) rot=(0,0,1;0rad)
  AttachmentSupport = -> [XY_Plane002]
  Length = 61.1129
  MapMode = 5
  Placement = pos=(0,0,89) rot=(0,0,1;0rad)
  ResizeMode = 0
  Width = 72.8606
  expr: .AttachmentOffset.Base.z = <<Monitor Chassis Parameters>>.GSTowerSecondFloorHeight + <<Monitor Chassis Parameters>>.GSTowerFloorThickness
FEATURE [PartDesign::Plane] DatumPlane004  label="Third Floor DatumPlane"
  AttachmentOffset = pos=(0,0,179) rot=(0,0,1;0rad)
  AttachmentSupport = -> [XY_Plane002]
  Length = 61.1129
  MapMode = 5
  Placement = pos=(0,0,179) rot=(0,0,1;0rad)
  ResizeMode = 0
  Width = 72.8606
  expr: .AttachmentOffset.Base.z = <<Monitor Chassis Parameters>>.GSTowerThirdFloorHeight + <<Monitor Chassis Parameters>>.GSTowerFloorThickness
FEATURE [Sketcher::SketchObject] Sketch011  label="Third Floor Holes Sketch"
  ArcFitTolerance = 1e-06
  AttachmentSupport = -> [DatumPlane004]
  FullyConstrained = true
  MakeInternals = false
  MapMode = 5
  Placement = pos=(0,0,179) rot=(0,0,1;0rad)
  expr: Constraints[1] = 2 + 0.5 * <<Monitor Chassis Parameters>>.GSTowerThirdFloorDepth
  expr: Constraints[2] = <<Monitor Chassis Parameters>>.GSMonitorFloorCameraMountHoleDiameter
  sketch-geometry (1):
    g0: Circle CenterX=0 CenterY=-29.5 CenterZ=0 NormalX=0 NormalY=0 NormalZ=1 AngleXU=0 Radius=2.75
  constraints (3):
    c: PointOnObject(g0,g-2)
    c: DistanceY(g0,g-1) = 29.5
    c: Diameter(g0) = 5.5
FEATURE [PartDesign::Pocket] Pocket  label="Third Floor Holes Pocket"
  BaseFeature = -> Pad008
  Direction = (0,0,-1)
  Length = 5
  Length2 = 5
  Placement = pos=(0,0,0) rot=(1,0,0;1.5708rad)
  Profile = -> Sketch011
  ReferenceAxis = -> Sketch011 [N_Axis]
  Suppressed = false
  Type = 0
FEATURE [Sketcher::SketchObject] Sketch012  label="Second Floor Holes Sketch"
  ArcFitTolerance = 1e-06
  AttachmentSupport = -> [DatumPlane003]
  FullyConstrained = true
  MakeInternals = false
  MapMode = 2
  Placement = pos=(0,0,89) rot=(0,0,1;0rad)
  expr: Constraints[0] = <<Monitor Chassis Parameters>>.GSMonitorFloorCameraMountHoleDiameter
  expr: Constraints[2] = 12 + 0.4 * <<Monitor Chassis Parameters>>.GSTowerSecondFloorDepth
  sketch-geometry (1):
    g0: Circle CenterX=0 CenterY=-34 CenterZ=0 NormalX=0 NormalY=0 NormalZ=1 AngleXU=0 Radius=2.75
  constraints (3):
    c: Diameter(g0) = 5.5
    c: Vertical(g-1,g0)
    c: DistanceY(g0,g-1) = 34
FEATURE [PartDesign::Pocket] Pocket001  label="Second Floor Holes Pocket"
  BaseFeature = -> Pocket
  Direction = (0,0,-1)
  Length = 5
  Length2 = 5
  Placement = pos=(0,0,0) rot=(1,0,0;1.5708rad)
  Profile = -> Sketch012
  ReferenceAxis = -> Sketch012 [N_Axis]
  Suppressed = false
  Type = 0
FEATURE [Sketcher::SketchObject] Sketch013  label="First Floor Holes Sketch"
  ArcFitTolerance = 1e-06
  AttachmentSupport = -> [DatumPlane002]
  FullyConstrained = true
  MakeInternals = false
  MapMode = 5
  Placement = pos=(0,0,9) rot=(0,0,1;0rad)
  expr: Constraints[0] = <<Monitor Chassis Parameters>>.GSMonitorFloorCameraMountHoleDiameter
  expr: Constraints[2] = 0.5 * <<Monitor Chassis Parameters>>.GSTowerFirstFloorDepth
  sketch-geometry (1):
    g0: Circle CenterX=0 CenterY=-25 CenterZ=0 NormalX=0 NormalY=0 NormalZ=1 AngleXU=0 Radius=2.75
  constraints (3):
    c: Diameter(g0) = 5.5
    c: Vertical(g0,g-1)
    c: DistanceY(g0,g-1) = 25
FEATURE [PartDesign::Pocket] Pocket002  label="First Floor Holes Pocket"
  BaseFeature = -> Pocket001
  Direction = (0,0,-1)
  Length = 5
  Length2 = 5
  Placement = pos=(0,0,0) rot=(1,0,0;1.5708rad)
  Profile = -> Sketch013
  ReferenceAxis = -> Sketch013 [N_Axis]
  Suppressed = false
  Type = 0
FEATURE [Sketcher::SketchObject] Sketch014  label="Shank Shield Riser Sketch"
  ArcFitTolerance = 1e-06
  AttachmentSupport = -> [XZ_Plane002]
  FullyConstrained = true
  MakeInternals = false
  MapMode = 5
  Placement = pos=(0,0,0) rot=(1,0,0;1.5708rad)
  expr: Constraints[0] = 3 * <<Monitor Chassis Parameters>>.GSM4TappingScrewHoleDiameter
  expr: Constraints[1] = <<Monitor Chassis Parameters>>.GSTowerFourthFloorHeight - 1.5 * <<Monitor Chassis Parameters>>.GSM4TappingScrewHoleDiameter
  expr: Constraints[2] = 0.5 * <<Monitor Chassis Parameters>>.GSBackPlateWidth - 1.5 * <<Monitor Chassis Parameters>>.GSM4TappingScrewHoleDiameter
  expr: Constraints[3] = 3 * <<Monitor Chassis Parameters>>.GSM4TappingScrewHoleDiameter
  expr: Constraints[5] = <<Monitor Chassis Parameters>>.GSBackPlateWidth - 3 * <<Monitor Chassis Parameters>>.GSM4TappingScrewHoleDiameter
  sketch-geometry (2):
    g0: Circle CenterX=-49.7 CenterY=249.9 CenterZ=0 NormalX=0 NormalY=0 NormalZ=1 AngleXU=0 Radius=5.1
    g1: Circle CenterX=49.7 CenterY=249.9 CenterZ=0 NormalX=0 NormalY=0 NormalZ=1 AngleXU=0 Radius=5.1
  constraints (6):
    c: Diameter(g0) = 10.2
    c: DistanceY(g-1,g0) = 249.9
    c: DistanceX(g0,g-1) = 49.7
    c: Diameter(g1) = 10.2
    c: Horizontal(g0,g1)
    c: DistanceX(g0,g1) = 99.4
FEATURE [PartDesign::Pad] Pad009  label="Shank Shield Riser Pad"
  BaseFeature = -> Pocket002
  Direction = (0,-1,2e-16)
  Length = 89.65
  Length2 = 10
  Placement = pos=(0,0,0) rot=(1,0,0;1.5708rad)
  Profile = -> Sketch014
  ReferenceAxis = -> Sketch014 [N_Axis]
  Suppressed = false
  Type = 0
  expr: Length = 1 + <<Monitor Chassis Parameters>>.GSBasePowerBoxTowerBackOffsetFromFront - <<Monitor Chassis Parameters>>.GSShankShieldThickness - <<Monitor Chassis Parameters>>.GSBackPlateThickness - 3 * <<Monitor Chassis Parameters>>.GSBasePowerBoxSideThickness
FEATURE [PartDesign::Plane] DatumPlane005  label="Shank Shield Riser Front DatumPlane005"
  AttachmentSupport = -> [Pad009]
  Length = 68.9737
  MapMode = 5
  Placement = pos=(0,-89.65,0) rot=(1,0,0;1.5708rad)
  ResizeMode = 0
  Width = 198.974
FEATURE [Sketcher::SketchObject] Sketch015  label="Shank Shield Riser Screw Holes Sketch"
  ArcFitTolerance = 1e-06
  AttachmentSupport = -> [DatumPlane005]
  FullyConstrained = true
  MakeInternals = false
  MapMode = 5
  Placement = pos=(0,-89.65,0) rot=(1,0,0;1.5708rad)
  expr: Constraints[0] = 0.5 * <<Monitor Chassis Parameters>>.GSBackPlateWidth - 1.5 * <<Monitor Chassis Parameters>>.GSM4TappingScrewHoleDiameter
  expr: Constraints[1] = <<Monitor Chassis Parameters>>.GSM4TappingScrewHoleDiameter
  expr: Constraints[3] = <<Monitor Chassis Parameters>>.GSTowerFourthFloorHeight - 1.5 * <<Monitor Chassis Parameters>>.GSM4TappingScrewHoleDiameter
  expr: Constraints[4] = 0.5 * <<Monitor Chassis Parameters>>.GSBackPlateWidth - 1.5 * <<Monitor Chassis Parameters>>.GSM4TappingScrewHoleDiameter
  expr: Constraints[5] = <<Monitor Chassis Parameters>>.GSM4TappingScrewHoleDiameter
  sketch-geometry (2):
    g0: Circle CenterX=-49.7 CenterY=249.9 CenterZ=0 NormalX=0 NormalY=0 NormalZ=1 AngleXU=0 Radius=1.7
    g1: Circle CenterX=49.7 CenterY=249.9 CenterZ=0 NormalX=0 NormalY=0 NormalZ=1 AngleXU=0 Radius=1.7
  constraints (6):
    c: DistanceX(g0,g-1) = 49.7
    c: Diameter(g0) = 3.4
    c: Horizontal(g0,g1)
    c: DistanceY(g-1,g0) = 249.9
    c: DistanceX(g-1,g1) = 49.7
    c: Diameter(g1) = 3.4
FEATURE [PartDesign::Pocket] Pocket003  label="Shank Shield Riser Screw Holes Pocket"
  BaseFeature = -> Pad009
  Direction = (0,1,-2e-16)
  Length = 14
  Length2 = 5
  Placement = pos=(0,0,0) rot=(1,0,0;1.5708rad)
  Profile = -> Sketch015
  ReferenceAxis = -> Sketch015 [N_Axis]
  Suppressed = false
  Type = 0
  expr: Length = 14
FEATURE [PartDesign::Plane] DatumPlane006  label="Fourth Floor DatumPlane"
  AttachmentOffset = pos=(0,0,259) rot=(0,0,1;0rad)
  AttachmentSupport = -> [XY_Plane002]
  Length = 61.1129
  MapMode = 5
  Placement = pos=(0,0,259) rot=(0,0,1;0rad)
  ResizeMode = 0
  Width = 72.8606
  expr: .AttachmentOffset.Base.z = <<Monitor Chassis Parameters>>.GSTowerFourthFloorHeight + <<Monitor Chassis Parameters>>.GSTowerFloorThickness
FEATURE [Sketcher::SketchObject] Sketch016  label="Fourth Floor Cutout Sketch"
  ArcFitTolerance = 1e-06
  AttachmentSupport = -> [DatumPlane006]
  FullyConstrained = false
  MakeInternals = false
  MapMode = 5
  Placement = pos=(0,0,259) rot=(0,0,1;0rad)
  sketch-geometry (4):
    g0: LineSegment StartX=-44.9421 StartY=-8.20433 StartZ=0 EndX=-44.9421 EndY=-45.1974 EndZ=0
    g1: LineSegment StartX=-44.9421 StartY=-45.1974 StartZ=0 EndX=49.6477 EndY=-45.1974 EndZ=0
    g2: LineSegment StartX=49.6477 StartY=-45.1974 StartZ=0 EndX=49.6477 EndY=-8.20433 EndZ=0
    g3: LineSegment StartX=49.6477 StartY=-8.20433 StartZ=0 EndX=-44.9421 EndY=-8.20433 EndZ=0
  constraints (8):
    c: Coincident(g0,g1)
    c: Coincident(g1,g2)
    c: Coincident(g2,g3)
    c: Coincident(g3,g0)
    c: Vertical(g0)
    c: Vertical(g2)
    c: Horizontal(g1)
    c: Horizontal(g3)
FEATURE [PartDesign::Plane] DatumPlane007  label="Suggested Backplate Split DatumPlane"
  AttachmentOffset = pos=(0,0,120) rot=(0,0,1;0rad)
  AttachmentSupport = -> [XY_Plane001]
  Length = 119.016
  MapMode = 5
  Placement = pos=(0,0,120) rot=(0,0,1;0rad)
  ResizeMode = 0
  Width = 67.0538
  expr: .AttachmentOffset.Base.z = 120
FEATURE [PartDesign::Plane] DatumPlane008  label="Suggested Frontplate Split DatumPlane"
  AttachmentOffset = pos=(0,0,155) rot=(0,0,1;0rad)
  AttachmentSupport = -> [XY_Plane002]
  Length = 61.1129
  MapMode = 5
  Placement = pos=(0,0,155) rot=(0,0,1;0rad)
  ResizeMode = 0
  Width = 72.8606
  expr: .AttachmentOffset.Base.z = 155
FEATURE [PartDesign::Body] Body001  label="Frontplate Body"
  AllowCompound = false
  Group = -> [Sketch005,Pad004,Sketch007,Pad006,Sketch008,Hole001,DatumPlane001,Sketch009,Pad007,Mirrored001,Sketch010,Pad008,DatumPlane002,DatumPlane003,DatumPlane004,Sketch011,Pocket,Sketch012,Pocket001,Sketch013,Pocket002,Sketch014,Pad009,DatumPlane005,Sketch015,Pocket003,DatumPlane006,Sketch016,DatumPlane008]
  Origin = -> Origin002
  Placement = pos=(0.1,5,0) rot=(0,0,1;3.14159rad)
  Tip = -> Pocket003
FEATURE [Sketcher::SketchObject] Sketch017  label="Tower Layer Join Screw Holes Sketch"
  ArcFitTolerance = 1e-06
  AttachmentSupport = -> [XZ_Plane001]
  FullyConstrained = true
  MakeInternals = false
  MapMode = 5
  Placement = pos=(0,0,0) rot=(1,0,0;1.5708rad)
  expr: Constraints[0] = <<Monitor Chassis Parameters>>.GSTowerLayerJoinScrewDiameter
  expr: Constraints[1] = <<Monitor Chassis Parameters>>.GSM2TappingScrewHoleDiameter
  expr: Constraints[22] = 0.5 * <<Monitor Chassis Parameters>>.GSBackPlateWidth - <<Monitor Chassis Parameters>>.GSTowerLayerJoinScrewInset
  expr: Constraints[23] = 0.5 * <<Monitor Chassis Parameters>>.GSBackPlateWidth - <<Monitor Chassis Parameters>>.GSTowerLayerJoinScrewInset
  expr: Constraints[24] = <<Monitor Chassis Parameters>>.GSTowerLayerJoinScrewHeightFromFoot_1
  expr: Constraints[25] = <<Monitor Chassis Parameters>>.GSTowerLayerJoinScrewHeightFromFoot_2
  expr: Constraints[26] = <<Monitor Chassis Parameters>>.GSTowerLayerJoinScrewHeightFromFoot_3
  expr: Constraints[27] = <<Monitor Chassis Parameters>>.GSTowerLayerJoinScrewHeightFromFoot_4
  expr: Constraints[28] = <<Monitor Chassis Parameters>>.GSTowerLayerJoinScrewHeightFromFoot_5
  expr: Constraints[29] = <<Monitor Chassis Parameters>>.GSM2TappingScrewHoleDiameter
  expr: Constraints[2] = <<Monitor Chassis Parameters>>.GSM2TappingScrewHoleDiameter
  expr: Constraints[30] = <<Monitor Chassis Parameters>>.GSM2TappingScrewHoleDiameter
  expr: Constraints[35] = <<Monitor Chassis Parameters>>.GSTowerLayerJoinScrewHeightFromFoot_6
  expr: Constraints[3] = <<Monitor Chassis Parameters>>.GSM2TappingScrewHoleDiameter
  expr: Constraints[4] = <<Monitor Chassis Parameters>>.GSM2TappingScrewHoleDiameter
  expr: Constraints[5] = <<Monitor Chassis Parameters>>.GSM2TappingScrewHoleDiameter
  expr: Constraints[6] = <<Monitor Chassis Parameters>>.GSM2TappingScrewHoleDiameter
  expr: Constraints[7] = <<Monitor Chassis Parameters>>.GSM2TappingScrewHoleDiameter
  expr: Constraints[8] = <<Monitor Chassis Parameters>>.GSM2TappingScrewHoleDiameter
  expr: Constraints[9] = <<Monitor Chassis Parameters>>.GSM2TappingScrewHoleDiameter
  sketch-geometry (12):
    g0: Circle CenterX=44.8 CenterY=170 CenterZ=0 NormalX=0 NormalY=0 NormalZ=1 AngleXU=0 Radius=0.855
    g1: Circle CenterX=-44.8 CenterY=145 CenterZ=0 NormalX=0 NormalY=0 NormalZ=1 AngleXU=0 Radius=0.855
    g2: Circle CenterX=44.8 CenterY=145 CenterZ=0 NormalX=0 NormalY=0 NormalZ=1 AngleXU=0 Radius=0.855
    g3: Circle CenterX=-44.8 CenterY=125 CenterZ=0 NormalX=0 NormalY=0 NormalZ=1 AngleXU=0 Radius=0.855
    g4: Circle CenterX=-44.8 CenterY=104 CenterZ=0 NormalX=0 NormalY=0 NormalZ=1 AngleXU=0 Radius=0.855
    g5: Circle CenterX=44.8 CenterY=125 CenterZ=0 NormalX=0 NormalY=0 NormalZ=1 AngleXU=0 Radius=0.855
    g6: Circle CenterX=44.8 CenterY=104 CenterZ=0 NormalX=0 NormalY=0 NormalZ=1 AngleXU=0 Radius=0.855
    g7: Circle CenterX=-44.8 CenterY=30 CenterZ=0 NormalX=0 NormalY=0 NormalZ=1 AngleXU=0 Radius=0.855
    g8: Circle CenterX=44.8 CenterY=30 CenterZ=0 NormalX=0 NormalY=0 NormalZ=1 AngleXU=0 Radius=0.855
    g9: Circle CenterX=-44.8 CenterY=170 CenterZ=0 NormalX=0 NormalY=0 NormalZ=1 AngleXU=0 Radius=0.855
    g10: Circle CenterX=-44.8 CenterY=230 CenterZ=0 NormalX=0 NormalY=0 NormalZ=1 AngleXU=0 Radius=0.855
    g11: Circle CenterX=44.8 CenterY=230 CenterZ=0 NormalX=0 NormalY=0 NormalZ=1 AngleXU=0 Radius=0.855
  constraints (36):
    c: Diameter(g0) = 1.71
    c: Diameter(g1) = 1.71
    c: Diameter(g2) = 1.71
    c: Diameter(g3) = 1.71
    c: Diameter(g4) = 1.71
    c: Diameter(g5) = 1.71
    c: Diameter(g6) = 1.71
    c: Diameter(g7) = 1.71
    c: Diameter(g8) = 1.71
    c: Diameter(g9) = 1.71
    c: Vertical(g9,g1)
    c: Vertical(g1,g3)
    c: Vertical(g4,g3)
    c: Vertical(g7,g4)
    c: Vertical(g8,g6)
    c: Vertical(g6,g5)
    c: Vertical(g5,g2)
    c: Vertical(g0,g2)
    c: Horizontal(g2,g1)
    c: Horizontal(g3,g5)
    c: Horizontal(g4,g6)
    c: Horizontal(g7,g8)
    c: DistanceX(g7,g-1) = 44.8
    c: DistanceX(g-1,g8) = 44.8
    c: DistanceY(g-1,g7) = 30
    c: DistanceY(g-1,g4) = 104
    c: DistanceY(g-1,g3) = 125
    c: DistanceY(g-1,g1) = 145
    c: DistanceY(g-1,g9) = 170
    c: Diameter(g11) = 1.71
    c: Diameter(g10) = 1.71
    c: Horizontal(g9,g0)
    c: Vertical(g0,g11)
    c: Horizontal(g10,g11)
    c: Vertical(g10,g9)
    c: DistanceY(g-1,g10) = 230
FEATURE [PartDesign::Hole] Hole002  label="Plate Connection Holes"
  BaseFeature = -> Mirrored
  CustomThreadClearance = 0
  Depth = 25
  DepthType = 0
  Diameter = 1.71
  DrillForDepth = false
  DrillPoint = 1
  DrillPointAngle = 118
  HoleCutCountersinkAngle = 90
  HoleCutCustomValues = false
  HoleCutDepth = 0
  HoleCutDiameter = 3.5
  HoleCutType = 2
  ModelThread = false
  Placement = pos=(0,0,0) rot=(1,0,0;1.5708rad)
  Profile = -> Sketch017
  Suppressed = false
  Tapered = false
  TaperedAngle = 90
  ThreadClass = 0
  ThreadDepth = 25
  ThreadDepthType = 0
  ThreadDirection = 0
  ThreadFit = 0
  ThreadSize = 0
  ThreadType = 0
  Threaded = false
  UseCustomThreadClearance = false
  expr: Diameter = <<Monitor Chassis Parameters>>.GSTowerLayerJoinScrewDiameter
  expr: HoleCutDiameter = <<Monitor Chassis Parameters>>.GSM2BoltCountersinkDiameter
FEATURE [Part::Part2DObjectPython] ShapeString  label="Direction and ID ShapeString"  # Draft 2D object (typed FeaturePython)
  FontFile = <path>
  Fuse = false
  Justification = 6
  JustificationReference = 0
  KeepLeftMargin = false
  MakeFace = true
  ObliqueAngle = 0
  Placement = pos=(46.66,-0.3,5.22) rot=(0.57735,-0.57735,0.57735;2.0944rad)
  ScaleToSize = true
  Size = 5
  String = PiTrac                --> UP                                               --> UP
  Tracking = 0
FEATURE [PartDesign::Pocket] Pocket004  label="Direction and ID Pocket"
  BaseFeature = -> Hole002
  Direction = (1e-16,1,-2e-16)
  Length = 1
  Length2 = 5
  Placement = pos=(0,0,0) rot=(1,0,0;1.5708rad)
  Profile = -> ShapeString
  ReferenceAxis = -> ShapeString [N_Axis]
  Suppressed = false
  Type = 0
FEATURE [PartDesign::Body] Body  label="Backplate Body"
  AllowCompound = false
  Group = -> [Sketch,Sketch001,Pad,Pad001,Sketch002,Pad002,Sketch003,Hole,DatumPlane,Sketch004,Pad003,Mirrored,DatumPlane007,Sketch017,Hole002,ShapeString,Pocket004]
  Origin = -> Origin001
  Placement = pos=(0.2,-1,0) rot=(0,0,1;0rad)
  Tip = -> Pocket004
FEATURE [App::Part] Part  label="Tower Part -V2  Connector Board Variant"
  Group = -> [Body,Body001]
  Origin = -> Origin
FEATURE [Part::Feature] Part__Feature  label="SOT-23-5"
  Placement = pos=(110.45,-64.25,1.6096) rot=(0,0,-1;1.5708rad)
  shape: bbox 2.9 x 2.8 x 1.55 mm, 102 faces (baked)
FEATURE [Part::Feature] Part__Feature001  label="SOT-23"
  Placement = pos=(123,-123.75,1.6096) rot=(0,0,1;3.14159rad)
  shape: bbox 2.5 x 3 x 1.2 mm, 69 faces (baked)
FEATURE [Part::Feature] Part__Feature002  label="C_0603_1608Metric"
  Placement = pos=(134,-128.387,1.6096) rot=(0,0,-1;1.5708rad)
  shape: bbox 0.8 x 1.6 x 0.8 mm, 28 faces (baked)
FEATURE [Part::Feature] Part__Feature003  label="C_0603_1608Metric001"
  Placement = pos=(128.5,-65,1.6096) rot=(0,0,-1;1.5708rad)
  shape: bbox 0.8 x 1.6 x 0.8 mm, 28 faces (baked)
FEATURE [Part::Feature] Part__Feature004  label="C_0603_1608Metric002"
  Placement = pos=(130,-55,1.6096) rot=(0,0,1;3.14159rad)
  shape: bbox 1.6 x 0.8 x 0.8 mm, 28 faces (baked)
FEATURE [Part::Feature] Part__Feature005  label="L_Radial_D8.7mm_P5.00mm_Fastron_07HCP"
  Placement = pos=(115.98,-108.5,1.6096) rot=(0,0,-1;1.5708rad)
  shape: bbox 8.7 x 8.7 x 13.05 mm, 27 faces (baked)
FEATURE [Part::Feature] Part__Feature006  label="C_0603_1608Metric003"
  Placement = pos=(116.5,-99.5,1.6096) rot=(0,0,1;1.5708rad)
  shape: bbox 0.8 x 1.6 x 0.8 mm, 28 faces (baked)
FEATURE [Part::Feature] Part__Feature007  label="C_0603_1608Metric004"
  Placement = pos=(135.75,-56.5,1.6096) rot=(0,0,1;1.5708rad)
  shape: bbox 0.8 x 1.6 x 0.8 mm, 28 faces (baked)
FEATURE [Part::Feature] Part__Feature008  label="C_0805_2012Metric"
  Placement = pos=(111.25,-119,1.6096) rot=(0,0,-1;1.5708rad)
  shape: bbox 1.25 x 2 x 1.25 mm, 28 faces (baked)
FEATURE [Part::Feature] Part__Feature009  label="R_0603_1608Metric"
  Placement = pos=(130.5,-131.5,1.6096) rot=(0,0,1;0rad)
  shape: bbox 1.6 x 0.8 x 0.45 mm, 26 faces (baked)
FEATURE [Part::Feature] Part__Feature010  label="R_0603_1608Metric001"
  Placement = pos=(136.5,-96.75,1.6096) rot=(0,0,1;1.5708rad)
  shape: bbox 0.8 x 1.6 x 0.45 mm, 26 faces (baked)
FEATURE [Part::Feature] Part__Feature011  label="R_0603_1608Metric002"
  Placement = pos=(124.5,-83,1.6096) rot=(0,0,-1;1.5708rad)
  shape: bbox 0.8 x 1.6 x 0.45 mm, 26 faces (baked)
FEATURE [Part::Feature] Part__Feature012  label="C_0603_1608Metric005"
  Placement = pos=(126.5,-86.5,1.6096) rot=(0,0,-1;1.5708rad)
  shape: bbox 0.8 x 1.6 x 0.8 mm, 28 faces (baked)
FEATURE [Part::Feature] Part__Feature013  label="C_0603_1608Metric006"
  Placement = pos=(129.5,-128.387,1.6096) rot=(0,0,1;1.5708rad)
  shape: bbox 0.8 x 1.6 x 0.8 mm, 28 faces (baked)
FEATURE [Part::Feature] Part__Feature014  label="CP_Radial_D10.0mm_P5.00mm"
  Placement = pos=(148,-119.632,1.6096) rot=(0,0,-1;1.5708rad)
  shape: bbox 12.78 x 12.36 x 12 mm, 48 faces (baked)
FEATURE [Part::Feature] Part__Feature015  label="R_0603_1608Metric003"
  Placement = pos=(116.25,-132.792,1.6096) rot=(0,0,1;1.5708rad)
  shape: bbox 0.8 x 1.6 x 0.45 mm, 26 faces (baked)
FEATURE [Part::Feature] Part__Feature016  label="R_0603_1608Metric004"
  Placement = pos=(134.75,-135.5,1.6096) rot=(0,0,1;3.14159rad)
  shape: bbox 1.6 x 0.8 x 0.45 mm, 26 faces (baked)
FEATURE [Part::Feature] Part__Feature017  label="SOT-23-6"
  Placement = pos=(132.137,-58.2,1.6096) rot=(0,0,1;0rad)
  shape: bbox 2.8 x 2.9 x 1.55 mm, 117 faces (baked)
FEATURE [Part::Feature] Part__Feature018  label="C_0603_1608Metric007"
  Placement = pos=(117.5,-135.75,1.6096) rot=(0,0,1;3.14159rad)
  shape: bbox 1.6 x 0.8 x 0.8 mm, 28 faces (baked)
FEATURE [Part::Feature] Part__Feature019  label="R_0603_1608Metric005"
  Placement = pos=(119.5,-100.25,1.6096) rot=(0,0,1;0rad)
  shape: bbox 1.6 x 0.8 x 0.45 mm, 26 faces (baked)
FEATURE [Part::Feature] Part__Feature020  label="SOIC-8_3.9x4.9mm_P1.27mm"
  Placement = pos=(116.115,-120.725,1.6096) rot=(0,0,1;1.5708rad)
  shape: bbox 4.9 x 6 x 1.75 mm, 147 faces (baked)
FEATURE [Part::Feature] Part__Feature021  label="SOT-23-3"
  Placement = pos=(121.75,-136.75,1.6096) rot=(0,0,1;1.5708rad)
  shape: bbox 3 x 2.5 x 1.2 mm, 69 faces (baked)
FEATURE [Part::Feature] Part__Feature022  label="C_0603_1608Metric008"
  Placement = pos=(129.75,-125.25,1.6096) rot=(0,0,1;0rad)
  shape: bbox 1.6 x 0.8 x 0.8 mm, 28 faces (baked)
FEATURE [Part::Feature] Part__Feature023  label="D_SOD-123"
  Placement = pos=(120,-76.5,1.6096) rot=(0,0,1;3.14159rad)
  shape: bbox 3.8 x 1.6 x 1.26 mm, 59 faces (baked)
FEATURE [Part::Feature] Part__Feature024  label="R_0603_1608Metric006"
  Placement = pos=(137,-61.5,1.6096) rot=(0,0,-1;1.5708rad)
  shape: bbox 0.8 x 1.6 x 0.45 mm, 26 faces (baked)
FEATURE [Part::Feature] Part__Feature025  label="R_0805_2012Metric"
  Placement = pos=(115.615,-127,1.6096) rot=(0,0,1;1.5708rad)
  shape: bbox 1.2 x 2 x 0.45 mm, 26 faces (baked)
FEATURE [Part::Feature] Part__Feature026  label="C_0603_1608Metric009"
  Placement = pos=(130.5,-135.5,1.6096) rot=(0,0,1;3.14159rad)
  shape: bbox 1.6 x 0.8 x 0.8 mm, 28 faces (baked)
FEATURE [Part::Feature] Part__Feature027  label="R_0603_1608Metric007"
  Placement = pos=(126.5,-126,1.6096) rot=(0,0,1;1.5708rad)
  shape: bbox 0.8 x 1.6 x 0.45 mm, 26 faces (baked)
FEATURE [Part::Feature] Part__Feature028  label="C_0603_1608Metric010"
  Placement = pos=(126,-65,1.6096) rot=(0,0,-1;1.5708rad)
  shape: bbox 0.8 x 1.6 x 0.8 mm, 28 faces (baked)
FEATURE [Part::Feature] Part__Feature029  label="R_0603_1608Metric008"
  Placement = pos=(113.75,-138.25,1.6096) rot=(0,0,1;0rad)
  shape: bbox 1.6 x 0.8 x 0.45 mm, 26 faces (baked)
FEATURE [Part::Feature] Part__Feature030  label="C_0603_1608Metric011"
  Placement = pos=(123,-79.5,1.6096) rot=(0,0,1;0rad)
  shape: bbox 1.6 x 0.8 x 0.8 mm, 28 faces (baked)
FEATURE [Part::Feature] Part__Feature031  label="R_0603_1608Metric009"
  Placement = pos=(121.75,-140.25,1.6096) rot=(0,0,1;0rad)
  shape: bbox 1.6 x 0.8 x 0.45 mm, 26 faces (baked)
FEATURE [Part::Feature] Part__Feature032  label="R_0603_1608Metric010"
  Placement = pos=(113.75,-66,1.6096) rot=(0,0,1;1.5708rad)
  shape: bbox 0.8 x 1.6 x 0.45 mm, 26 faces (baked)
FEATURE [Part::Feature] Part__Feature033  label="SOT-23-007"
  Placement = pos=(118,-67.5,1.6096) rot=(0,0,1;1.5708rad)
  shape: bbox 3 x 2.5 x 1.2 mm, 69 faces (baked)
FEATURE [Part::Feature] Part__Feature034  label="R_0603_1608Metric011"
  Placement = pos=(137.25,-129.25,1.6096) rot=(0,0,1;0rad)
  shape: bbox 1.6 x 0.8 x 0.45 mm, 26 faces (baked)
FEATURE [Part::Feature] Part__Feature035  label="C_0603_1608Metric012"
  Placement = pos=(118.525,-132.792,1.6096) rot=(0,0,-1;1.5708rad)
  shape: bbox 0.8 x 1.6 x 0.8 mm, 28 faces (baked)
FEATURE [Part::Feature] Part__Feature036  label="R_0603_1608Metric012"
  Placement = pos=(134.75,-133.5,1.6096) rot=(0,0,1;0rad)
  shape: bbox 1.6 x 0.8 x 0.45 mm, 26 faces (baked)
FEATURE [Part::Feature] Part__Feature037  label="C_0603_1608Metric013"
  Placement = pos=(126.25,-135.5,1.6096) rot=(0,0,1;0rad)
  shape: bbox 1.6 x 0.8 x 0.8 mm, 28 faces (baked)
FEATURE [Part::Feature] Part__Feature038  label="C_0603_1608Metric014"
  Placement = pos=(113.5,-75.1375,1.6096) rot=(0,0,-1;1.5708rad)
  shape: bbox 0.8 x 1.6 x 0.8 mm, 28 faces (baked)
FEATURE [Part::Feature] Part__Feature039  label="R_0603_1608Metric013"
  Placement = pos=(131.75,-128.387,1.6096) rot=(0,0,1;1.5708rad)
  shape: bbox 0.8 x 1.6 x 0.45 mm, 26 faces (baked)
FEATURE [Part::Feature] Part__Feature040  label="C_1206_3216Metric"
  Placement = pos=(128,-112.75,1.6096) rot=(0,0,1;1.5708rad)
  shape: bbox 1.6 x 3.2 x 1.6 mm, 28 faces (baked)
FEATURE [Part::Feature] Part__Feature041  label="C_0603_1608Metric015"
  Placement = pos=(136.5,-92.75,1.6096) rot=(0,0,-1;1.5708rad)
  shape: bbox 0.8 x 1.6 x 0.8 mm, 28 faces (baked)
FEATURE [Part::Feature] Part__Feature042  label="SOIC-8_3.9x4.9mm_P1.27mm001"
  Placement = pos=(144,-94,1.6096) rot=(0,0,1;0rad)
  shape: bbox 6 x 4.9 x 1.75 mm, 147 faces (baked)
FEATURE [Part::Feature] Part__Feature043  label="SOT-23-008"
  Placement = pos=(132.5,-95,1.6096) rot=(0,0,1;3.14159rad)
  shape: bbox 2.8 x 2.9 x 1.55 mm, 117 faces (baked)
FEATURE [Part::Feature] Part__Feature044  label="SOT-23-009"
  Placement = pos=(113.5,-99.25,1.6096) rot=(0,0,1;1.5708rad)
  shape: bbox 3 x 2.5 x 1.2 mm, 69 faces (baked)
FEATURE [Part::Feature] Part__Feature045  label="R_0603_1608Metric014"
  Placement = pos=(144.75,-80,1.6096) rot=(0,0,1;1.5708rad)
  shape: bbox 0.8 x 1.6 x 0.45 mm, 26 faces (baked)
FEATURE [Part::Feature] Part__Feature046  label="CP_Radial_D10.0mm_P5.00mm001"
  Placement = pos=(135.25,-110.118,1.6096) rot=(0,0,1;1.5708rad)
  shape: bbox 12.78 x 12.36 x 12 mm, 48 faces (baked)
FEATURE [Part::Feature] Part__Feature047  label="R_0603_1608Metric015"
  Placement = pos=(137.5,-89.5,1.6096) rot=(0,0,1;3.14159rad)
  shape: bbox 1.6 x 0.8 x 0.45 mm, 26 faces (baked)
FEATURE [Part::Feature] Part__Feature048  label="R_0603_1608Metric016"
  Placement = pos=(123.25,-127,1.6096) rot=(0,0,1;3.14159rad)
  shape: bbox 1.6 x 0.8 x 0.45 mm, 26 faces (baked)
FEATURE [Part::Feature] Part__Feature049  label="SOIC-8_3.9x4.9mm_P1.27mm002"
  Placement = pos=(120.65,-62,1.6096) rot=(0,0,1;0rad)
  shape: bbox 6 x 4.9 x 1.75 mm, 147 faces (baked)
FEATURE [Part::Feature] Part__Feature050  label="C_0603_1608Metric016"
  Placement = pos=(124,-58,1.6096) rot=(0,0,1;0rad)
  shape: bbox 1.6 x 0.8 x 0.8 mm, 28 faces (baked)
FEATURE [Part::Feature] Part__Feature051  label="C_0603_1608Metric017"
  Placement = pos=(109.25,-142.5,1.6096) rot=(0,0,1;3.14159rad)
  shape: bbox 1.6 x 0.8 x 0.8 mm, 28 faces (baked)
FEATURE [Part::Feature] Part__Feature052  label="R_0603_1608Metric017"
  Placement = pos=(118.25,-128.25,1.6096) rot=(0,0,1;1.5708rad)
  shape: bbox 0.8 x 1.6 x 0.45 mm, 26 faces (baked)
FEATURE [Part::Feature] Part__Feature053  label="SOIC-8_3.9x4.9mm_P1.27mm003"
  Placement = pos=(123.775,-131.292,1.6096) rot=(0,0,1;3.14159rad)
  shape: bbox 6 x 4.9 x 1.75 mm, 147 faces (baked)
FEATURE [Part::Feature] Part__Feature054  label="R_0603_1608Metric018"
  Placement = pos=(134,-124.388,1.6096) rot=(0,0,1;1.5708rad)
  shape: bbox 0.8 x 1.6 x 0.45 mm, 26 faces (baked)
FEATURE [Part::Feature] Part__Feature055  label="R_1206_3216Metric"
  Placement = pos=(144,-88,1.6096) rot=(0,0,1;0rad)
  shape: bbox 3.2 x 1.6 x 0.55 mm, 26 faces (baked)
FEATURE [Part::Feature] Part__Feature056  label="SOT-23-010"
  Placement = pos=(114.25,-141.5,1.6096) rot=(0,0,1;3.14159rad)
  shape: bbox 2.8 x 2.9 x 1.55 mm, 102 faces (baked)
FEATURE [Part::Feature] Part__Feature057  label="R_0603_1608Metric019"
  Placement = pos=(128.5,-58,1.6096) rot=(0,0,1;1.5708rad)
  shape: bbox 0.8 x 1.6 x 0.45 mm, 26 faces (baked)
FEATURE [Part::Feature] Part__Feature058  label="PinHeader_1x03_P2.54mm_Vertical"
  Placement = pos=(147.75,-57.92,1.6096) rot=(0,0,1;0rad)
  shape: bbox 2.54 x 7.62 x 11.54 mm, 76 faces (baked)
FEATURE [Part::Feature] Part__Feature059  label="SOIC-8_3.9x4.9mm_P1.27mm004"
  Placement = pos=(119.5,-83.5,1.6096) rot=(0,0,1;0rad)
  shape: bbox 6 x 4.9 x 1.75 mm, 147 faces (baked)
FEATURE [Part::Feature] Part__Feature060  label="C_0603_1608Metric018"
  Placement = pos=(111.5,-69,1.6096) rot=(0,0,-1;1.5708rad)
  shape: bbox 0.8 x 1.6 x 0.8 mm, 28 faces (baked)
FEATURE [Part::Feature] Part__Feature061  label="R_0603_1608Metric020"
  Placement = pos=(114.5,-62.75,1.6096) rot=(0,0,1;3.14159rad)
  shape: bbox 1.6 x 0.8 x 0.45 mm, 26 faces (baked)
FEATURE [Part::Feature] Part__Feature062  label="R_0603_1608Metric021"
  Placement = pos=(121.5,-67.5,1.6096) rot=(0,0,1;1.5708rad)
  shape: bbox 0.8 x 1.6 x 0.45 mm, 26 faces (baked)
FEATURE [Part::Feature] Part__Feature063  label="D_SMA"
  Placement = pos=(125.25,-117.75,1.6096) rot=(0,0,1;3.14159rad)
  shape: bbox 5 x 2.7 x 2.22 mm, 41 faces (baked)
FEATURE [Part::Feature] Part__Feature064  label="R_0603_1608Metric022"
  Placement = pos=(119.088,-79.5,1.6096) rot=(0,0,1;3.14159rad)
  shape: bbox 1.6 x 0.8 x 0.45 mm, 26 faces (baked)
FEATURE [Part::Feature] Part__Feature065  label="C_0603_1608Metric019"
  Placement = pos=(124.5,-92.75,1.6096) rot=(0,0,1;0rad)
  shape: bbox 1.6 x 0.8 x 0.8 mm, 28 faces (baked)
FEATURE [Part::Feature] Part__Feature066  label="C_0603_1608Metric020"
  Placement = pos=(124.5,-86.5,1.6096) rot=(0,0,-1;1.5708rad)
  shape: bbox 0.8 x 1.6 x 0.8 mm, 28 faces (baked)
FEATURE [Part::Feature] Part__Feature067  label="C_0603_1608Metric021"
  Placement = pos=(113.5,-102.5,1.6096) rot=(0,0,1;0rad)
  shape: bbox 1.6 x 0.8 x 0.8 mm, 28 faces (baked)
FEATURE [Part::Feature] Part__Feature068  label="C_0603_1608Metric022"
  Placement = pos=(131.85,-98.25,1.6096) rot=(0,0,1;0rad)
  shape: bbox 1.6 x 0.8 x 0.8 mm, 28 faces (baked)
FEATURE [Part::Feature] Part__Feature069  label="SOT-23-011"
  Placement = pos=(123.5,-96.5,1.6096) rot=(0,0,1;1.5708rad)
  shape: bbox 2.9 x 2.8 x 1.55 mm, 117 faces (baked)
FEATURE [Part::Feature] Part__Feature070  label="R_0603_1608Metric023"
  Placement = pos=(130.5,-133.5,1.6096) rot=(0,0,1;3.14159rad)
  shape: bbox 1.6 x 0.8 x 0.45 mm, 26 faces (baked)
FEATURE [Part::Feature] Part__Feature071  label="R_0603_1608Metric024"
  Placement = pos=(126,-61.25,1.6096) rot=(0,0,-1;1.5708rad)
  shape: bbox 0.8 x 1.6 x 0.45 mm, 26 faces (baked)
FEATURE [Part::Feature] Part__Feature072  label="PiTrac Pi Connector_PCB"
  shape: bbox 60 x 100 x 1.524 mm, 99 faces (baked)
FEATURE [App::Part] PiTrac_Pi_Connector_1  label="PiTrac Pi Connector 1"
  Group = -> [Part__Feature,Part__Feature001,Part__Feature002,Part__Feature003,Part__Feature004,Part__Feature005,Part__Feature006,Part__Feature007,Part__Feature008,Part__Feature009,Part__Feature010,Part__Feature011,Part__Feature012,Part__Feature013,Part__Feature014,Part__Feature015,Part__Feature016,Part__Feature017,Part__Feature018,Part__Feature019,Part__Feature020,Part__Feature021,Part__Feature022,+50 more]
  Origin = -> Origin003
  Placement = pos=(-94.2002,-8.5,-52.5708) rot=(0.57735,-0.57735,0.57735;2.0944rad)
note: 1 file-system path scrubbed to <path> (originals preserved in the JSON sidecar)
